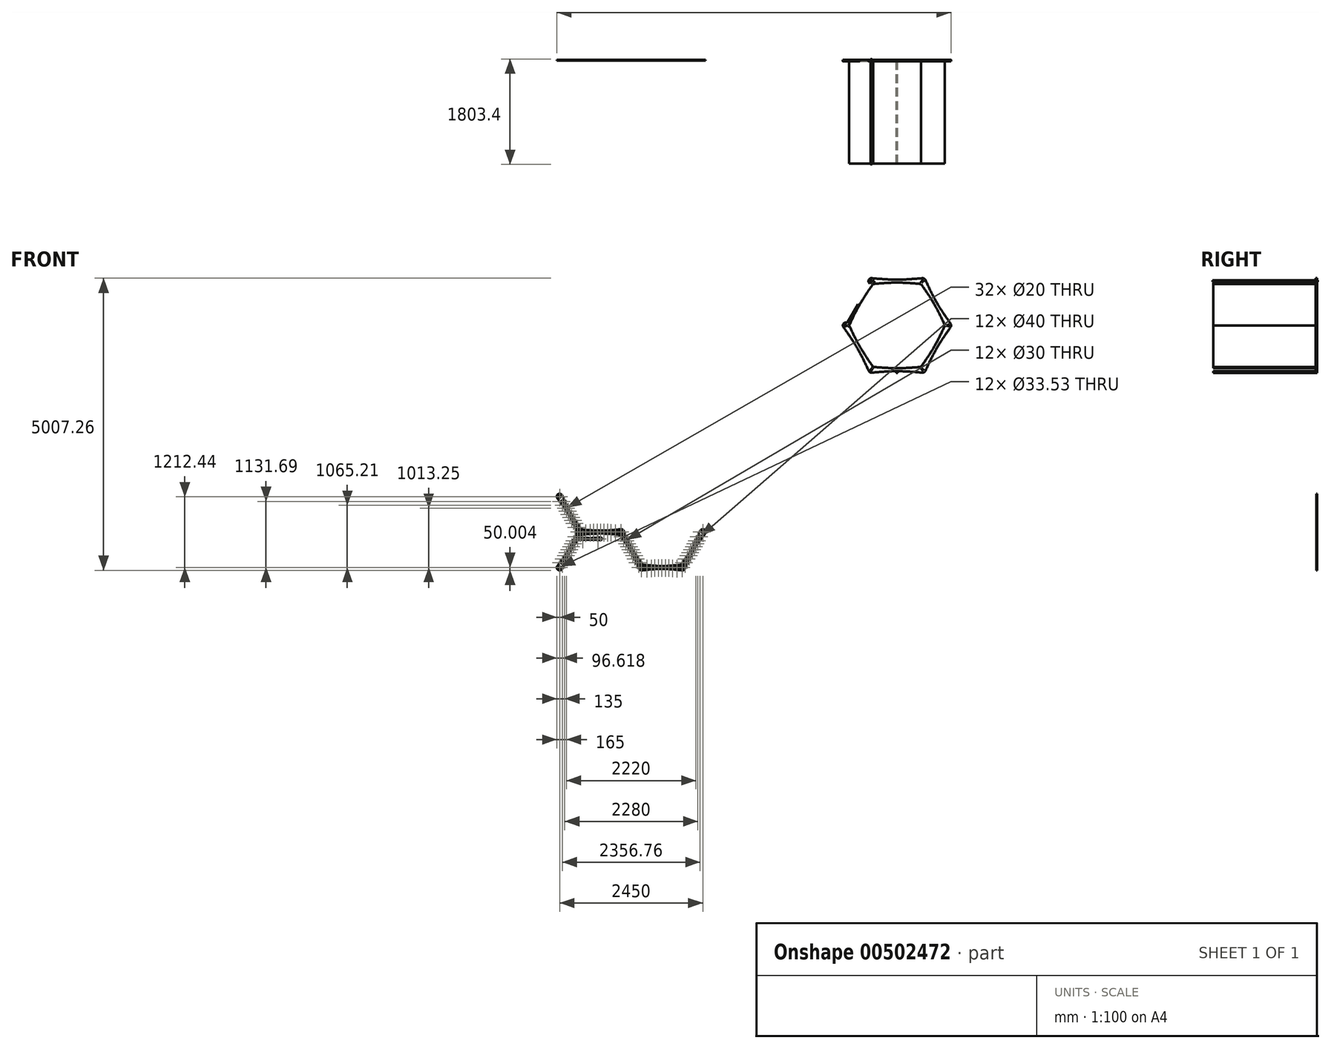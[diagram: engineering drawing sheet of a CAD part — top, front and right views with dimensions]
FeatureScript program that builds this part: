
annotation { "Feature Type Name" : "Feature", "Feature Type Description" : "" }
export const myFeature = defineFeature(function(context is Context, id is Id, definition is map)
    precondition{}
    {
        {
            var Q0;
            Q0=qCreatedBy(makeId("Front.planeOp"),FACE);
            var sketch = newSketch(context, id + "F0", { "sketchPlane" : qUnion([Q0])});
            skCircle(sketch, "E0", {"center": v(-63.33, -77.6) * mm, "radius": 25.4 * mm});
            skLineSegment(sketch, "E1", {"start": v(-63.33, -77.6) * mm, "end": v(286.67, -77.6) * mm});
            skLineSegment(sketch, "E2", {"start": v(-63.33, -77.6) * mm, "end": v(-88.73, -77.6) * mm});
            skLineSegment(sketch, "E3", {"start": v(-88.73, -77.6) * mm, "end": v(261.27, -77.6) * mm});
            skCircle(sketch, "E4", {"center": v(261.27, -77.6) * mm, "radius": 25.4 * mm});
            skLineSegment(sketch, "E5", {"start": v(86.27, -77.6) * mm, "end": v(86.27, -64.9) * mm});
            skLineSegment(sketch, "E6", {"start": v(86.27, -64.9) * mm, "end": v(86.27, -90.3) * mm});
            skCircle(sketch, "E7", {"center": v(0, 0) * mm, "radius": 25 * mm});
            skLineSegment(sketch, "E8", {"start": v(0, 0) * mm, "end": v(350, 0) * mm, "construction": true});
            skCircle(sketch, "E9", {"center": v(350, 0) * mm, "radius": 25 * mm});
            skLineSegment(sketch, "E10", {"start": v(175, 0) * mm, "end": v(175, -25) * mm, "construction": true});
            skFitSpline(sketch, "E11", {"points": [v(0, -25) * mm, v(175, -12.5) * mm, v(350, -25) * mm], "startDerivative": vector(350, 37.5) * mm, "endDerivative": vector(350, -37.5) * mm});
            skLineSegment(sketch, "E12", {"start": v(175, 0) * mm, "end": v(175, 25) * mm, "construction": true});
            skFitSpline(sketch, "E13", {"points": [v(0, 25) * mm, v(175, 12.5) * mm, v(350, 25) * mm], "startDerivative": vector(350, -37.5) * mm, "endDerivative": vector(350, 37.5) * mm});
            skCircle(sketch, "E14", {"center": v(350, 0) * mm, "radius": 8.38 * mm});
            skCircle(sketch, "E15", {"center": v(0, 0) * mm, "radius": 8.38 * mm});
            skCircle(sketch, "E16", {"center": v(175, 0) * mm, "radius": 5 * mm});
            skCircle(sketch, "E17.1.0.0", {"center": v(205, 0) * mm, "radius": 5 * mm});
            skCircle(sketch, "E17.2.0.0", {"center": v(235, 0) * mm, "radius": 5 * mm});
            skLineSegment(sketch, "E17.direction1", {"start": v(175, 0) * mm, "end": v(205, 0) * mm, "construction": true});
            skCircle(sketch, "E18.1.0.0", {"center": v(145, 0) * mm, "radius": 5 * mm});
            skCircle(sketch, "E18.2.0.0", {"center": v(115, 0) * mm, "radius": 5 * mm});
            skLineSegment(sketch, "E18.direction1", {"start": v(175, 0) * mm, "end": v(145, 0) * mm, "construction": true});
            skCircle(sketch, "E19", {"center": v(55, 0) * mm, "radius": 10 * mm});
            skCircle(sketch, "E20", {"center": v(85, 0) * mm, "radius": 7.5 * mm});
            skCircle(sketch, "E21.MirrorC", {"center": v(265, 0) * mm, "radius": 7.5 * mm});
            skCircle(sketch, "E22.MirrorC", {"center": v(295, 0) * mm, "radius": 10 * mm});
            skCircle(sketch, "E23", {"center": v(0, 115.33) * mm, "radius": 25 * mm});
            skLineSegment(sketch, "E24", {"start": v(0, 115.33) * mm, "end": v(350, 115.33) * mm, "construction": true});
            skCircle(sketch, "E25", {"center": v(350, 115.33) * mm, "radius": 25 * mm});
            skFitSpline(sketch, "E26", {"points": [v(0, 90.33) * mm, v(175, 102.83) * mm, v(350, 90.33) * mm], "startDerivative": vector(350, 37.5) * mm, "endDerivative": vector(350, -37.5) * mm});
            skFitSpline(sketch, "E27", {"points": [v(0, 140.33) * mm, v(175, 127.83) * mm, v(350, 140.33) * mm], "startDerivative": vector(350, -37.5) * mm, "endDerivative": vector(350, 37.5) * mm});
            skCircle(sketch, "E28", {"center": v(350, 115.33) * mm, "radius": 8.38 * mm});
            skCircle(sketch, "E29", {"center": v(0, 115.33) * mm, "radius": 8.38 * mm});
            skCircle(sketch, "E30", {"center": v(175, 115.33) * mm, "radius": 5 * mm});
            skCircle(sketch, "E31.1.0.0", {"center": v(205, 115.33) * mm, "radius": 5 * mm});
            skCircle(sketch, "E31.2.0.0", {"center": v(235, 115.33) * mm, "radius": 5 * mm});
            skLineSegment(sketch, "E31.direction1", {"start": v(175, 115.33) * mm, "end": v(205, 115.33) * mm, "construction": true});
            skCircle(sketch, "E32.1.0.0", {"center": v(145, 115.33) * mm, "radius": 5 * mm});
            skCircle(sketch, "E32.2.0.0", {"center": v(115, 115.33) * mm, "radius": 5 * mm});
            skLineSegment(sketch, "E32.direction1", {"start": v(175, 115.33) * mm, "end": v(145, 115.33) * mm, "construction": true});
            skCircle(sketch, "E33", {"center": v(46.62, 115.33) * mm, "radius": 10 * mm});
            skCircle(sketch, "E34", {"center": v(85, 115.33) * mm, "radius": 7.5 * mm});
            skCircle(sketch, "E35.MirrorC", {"center": v(265, 115.33) * mm, "radius": 7.5 * mm});
            skLineSegment(sketch, "E36", {"start": v(175, 102.83) * mm, "end": v(175, 127.83) * mm, "construction": true});
            skCircle(sketch, "E37.MirrorC", {"center": v(303.38, 115.33) * mm, "radius": 10 * mm});
            skCircle(sketch, "E38", {"center": v(-2662.95, -296.07) * mm, "radius": 25 * mm});
            skLineSegment(sketch, "E39", {"start": v(-2662.95, -296.07) * mm, "end": v(-2359.84, -121.07) * mm, "construction": true});
            skCircle(sketch, "E40", {"center": v(-2359.84, -121.07) * mm, "radius": 25 * mm});
            skFitSpline(sketch, "E41", {"points": [v(-2650.45, -317.72) * mm, v(-2505.15, -219.4) * mm, v(-2347.34, -142.72) * mm], "startDerivative": vector(284.36, 207.48) * mm, "endDerivative": vector(321.86, 142.52) * mm});
            skFitSpline(sketch, "E42", {"points": [v(-2675.45, -274.42) * mm, v(-2517.65, -197.74) * mm, v(-2372.34, -99.42) * mm], "startDerivative": vector(321.86, 142.52) * mm, "endDerivative": vector(284.36, 207.48) * mm});
            skCircle(sketch, "E43", {"center": v(-2359.84, -121.07) * mm, "radius": 8.38 * mm});
            skCircle(sketch, "E44", {"center": v(-2662.95, -296.07) * mm, "radius": 8.38 * mm});
            skCircle(sketch, "E45", {"center": v(-2511.4, -208.57) * mm, "radius": 5 * mm});
            skCircle(sketch, "E46.1.0.0", {"center": v(-2485.42, -193.57) * mm, "radius": 5 * mm});
            skCircle(sketch, "E46.2.0.0", {"center": v(-2459.43, -178.57) * mm, "radius": 5 * mm});
            skLineSegment(sketch, "E46.direction1", {"start": v(-2511.4, -208.57) * mm, "end": v(-2485.42, -193.57) * mm, "construction": true});
            skCircle(sketch, "E47.1.0.0", {"center": v(-2537.38, -223.57) * mm, "radius": 5 * mm});
            skCircle(sketch, "E47.2.0.0", {"center": v(-2563.36, -238.57) * mm, "radius": 5 * mm});
            skLineSegment(sketch, "E47.direction1", {"start": v(-2511.4, -208.57) * mm, "end": v(-2537.38, -223.57) * mm, "construction": true});
            skCircle(sketch, "E48", {"center": v(-2622.58, -272.76) * mm, "radius": 10 * mm});
            skCircle(sketch, "E49", {"center": v(-2589.34, -253.57) * mm, "radius": 7.5 * mm});
            skCircle(sketch, "E50.MirrorC", {"center": v(-2433.45, -163.57) * mm, "radius": 7.5 * mm});
            skLineSegment(sketch, "E51", {"start": v(-2505.15, -219.4) * mm, "end": v(-2517.65, -197.74) * mm, "construction": true});
            skCircle(sketch, "E52.MirrorC", {"center": v(-2400.21, -144.38) * mm, "radius": 10 * mm});
            skLineSegment(sketch, "E53.0", {"start": v(-2347.34, -142.72) * mm, "end": v(-2372.34, -99.42) * mm, "construction": true});
            skLineSegment(sketch, "E54", {"start": v(-2359.84, -121.07) * mm, "end": v(-2056.73, 53.93) * mm, "construction": true});
            skCircle(sketch, "E55", {"center": v(-2056.73, 53.93) * mm, "radius": 25 * mm});
            skFitSpline(sketch, "E56", {"points": [v(-2347.34, -142.72) * mm, v(-2202.04, -44.4) * mm, v(-2044.23, 32.28) * mm], "startDerivative": vector(284.36, 207.48) * mm, "endDerivative": vector(321.86, 142.52) * mm});
            skFitSpline(sketch, "E57", {"points": [v(-2372.34, -99.42) * mm, v(-2214.54, -22.74) * mm, v(-2069.23, 75.58) * mm], "startDerivative": vector(321.86, 142.52) * mm, "endDerivative": vector(284.36, 207.48) * mm});
            skCircle(sketch, "E58", {"center": v(-2056.73, 53.93) * mm, "radius": 8.38 * mm});
            skCircle(sketch, "E59", {"center": v(-2208.29, -33.57) * mm, "radius": 5 * mm});
            skCircle(sketch, "E60.1.0.0", {"center": v(-2182.3, -18.57) * mm, "radius": 5 * mm});
            skCircle(sketch, "E60.2.0.0", {"center": v(-2156.33, -3.57) * mm, "radius": 5 * mm});
            skLineSegment(sketch, "E60.direction1", {"start": v(-2208.29, -33.57) * mm, "end": v(-2182.3, -18.57) * mm, "construction": true});
            skCircle(sketch, "E61.1.0.0", {"center": v(-2234.27, -48.57) * mm, "radius": 5 * mm});
            skCircle(sketch, "E61.2.0.0", {"center": v(-2260.25, -63.57) * mm, "radius": 5 * mm});
            skLineSegment(sketch, "E61.direction1", {"start": v(-2208.29, -33.57) * mm, "end": v(-2234.27, -48.57) * mm, "construction": true});
            skCircle(sketch, "E62", {"center": v(-2319.47, -97.76) * mm, "radius": 10 * mm});
            skCircle(sketch, "E63", {"center": v(-2286.23, -78.57) * mm, "radius": 7.5 * mm});
            skCircle(sketch, "E64.MirrorC", {"center": v(-2130.34, 11.43) * mm, "radius": 7.5 * mm});
            skLineSegment(sketch, "E65", {"start": v(-2202.04, -44.4) * mm, "end": v(-2214.54, -22.74) * mm, "construction": true});
            skCircle(sketch, "E66.MirrorC", {"center": v(-2097.1, 30.62) * mm, "radius": 10 * mm});
            skLineSegment(sketch, "E67.0", {"start": v(-2044.23, 32.28) * mm, "end": v(-2069.23, 75.58) * mm, "construction": true});
            skSolve(sketch);
        }
        {
            var Q0;
            Q0=qCreatedBy(makeId("Front.planeOp"),FACE);
            var sketch = newSketch(context, id + "F1", { "sketchPlane" : qUnion([Q0])});
            skLineSegment(sketch, "E68.bottom", {"start": v(431.16, -314.1) * mm, "end": v(2869.56, -314.1) * mm});
            skLineSegment(sketch, "E68.top", {"start": v(431.16, 2124.3) * mm, "end": v(2869.56, 2124.3) * mm});
            skLineSegment(sketch, "E68.left", {"start": v(431.16, -314.1) * mm, "end": v(431.16, 2124.3) * mm});
            skLineSegment(sketch, "E68.right", {"start": v(2869.56, -314.1) * mm, "end": v(2869.56, 2124.3) * mm});
            skLineSegment(sketch, "E69", {"start": v(431.16, 905.1) * mm, "end": v(2869.56, 905.1) * mm, "construction": true});
            skCircle(sketch, "E70.cCircle", {"center": v(1197.59, 279.82) * mm, "radius": 593.92 * mm, "construction": true});
            skLineSegment(sketch, "E70.0", {"start": v(1540.49, -314.1) * mm, "end": v(854.69, -314.1) * mm, "construction": true});
            skLineSegment(sketch, "E70.1", {"start": v(854.69, -314.1) * mm, "end": v(511.79, 279.82) * mm, "construction": true});
            skLineSegment(sketch, "E70.2", {"start": v(511.79, 279.82) * mm, "end": v(854.69, 873.74) * mm, "construction": true});
            skLineSegment(sketch, "E70.3", {"start": v(854.69, 873.74) * mm, "end": v(1540.49, 873.74) * mm, "construction": true});
            skLineSegment(sketch, "E70.4", {"start": v(1540.49, 873.74) * mm, "end": v(1883.39, 279.82) * mm, "construction": true});
            skLineSegment(sketch, "E70.5", {"start": v(1883.39, 279.82) * mm, "end": v(1540.49, -314.1) * mm, "construction": true});
            skPoint(sketch, "E70.0.midPoint", {"position": v(1197.59, -314.1) * mm});
            skCircle(sketch, "E71.cCircle", {"center": v(2647.5, 295.5) * mm, "radius": 527.93 * mm, "construction": true});
            skLineSegment(sketch, "E71.0", {"start": v(3175.44, 600.3) * mm, "end": v(3175.44, -9.3) * mm});
            skLineSegment(sketch, "E71.1", {"start": v(3175.44, -9.3) * mm, "end": v(2647.5, -314.1) * mm});
            skLineSegment(sketch, "E71.2", {"start": v(2647.5, -314.1) * mm, "end": v(2119.58, -9.3) * mm});
            skLineSegment(sketch, "E71.3", {"start": v(2119.58, -9.3) * mm, "end": v(2119.58, 600.3) * mm});
            skLineSegment(sketch, "E71.4", {"start": v(2119.58, 600.3) * mm, "end": v(2647.5, 905.1) * mm});
            skLineSegment(sketch, "E71.5", {"start": v(2647.5, 905.1) * mm, "end": v(3175.44, 600.3) * mm});
            skPoint(sketch, "E71.0.midPoint", {"position": v(3175.44, 295.5) * mm});
            skCircle(sketch, "E72.cCircle", {"center": v(4442.22, 446.69) * mm, "radius": 703.9 * mm, "construction": true});
            skLineSegment(sketch, "E72.0", {"start": v(4442.22, -366.11) * mm, "end": v(3738.32, 40.29) * mm});
            skLineSegment(sketch, "E72.1", {"start": v(3738.32, 40.29) * mm, "end": v(3738.32, 853.09) * mm});
            skLineSegment(sketch, "E72.2", {"start": v(3738.32, 853.09) * mm, "end": v(4442.22, 1259.49) * mm});
            skLineSegment(sketch, "E72.3", {"start": v(4442.22, 1259.49) * mm, "end": v(5146.13, 853.09) * mm});
            skLineSegment(sketch, "E72.4", {"start": v(5146.13, 853.09) * mm, "end": v(5146.13, 40.29) * mm});
            skLineSegment(sketch, "E72.5", {"start": v(5146.13, 40.29) * mm, "end": v(4442.22, -366.11) * mm});
            skPoint(sketch, "E72.0.midPoint", {"position": v(4090.27, -162.91) * mm});
            skLineSegment(sketch, "E73.0", {"start": v(5146.13, 853.09) * mm, "end": v(4442.22, 1259.49) * mm});
            skLineSegment(sketch, "E73.1", {"start": v(4442.22, 1259.49) * mm, "end": v(4442.22, 2072.29) * mm});
            skLineSegment(sketch, "E73.2", {"start": v(4442.22, 2072.29) * mm, "end": v(5146.13, 2478.69) * mm});
            skLineSegment(sketch, "E73.3", {"start": v(5146.13, 2478.69) * mm, "end": v(5850.03, 2072.29) * mm});
            skLineSegment(sketch, "E73.4", {"start": v(5850.03, 2072.29) * mm, "end": v(5850.03, 1259.49) * mm});
            skLineSegment(sketch, "E73.5", {"start": v(5850.03, 1259.49) * mm, "end": v(5146.13, 853.09) * mm});
            skLineSegment(sketch, "E74.0", {"start": v(3175.44, 1819.5) * mm, "end": v(3175.44, 1209.9) * mm});
            skLineSegment(sketch, "E74.1", {"start": v(3175.44, 1209.9) * mm, "end": v(2647.5, 905.1) * mm});
            skLineSegment(sketch, "E74.2", {"start": v(2647.5, 905.1) * mm, "end": v(2119.58, 1209.9) * mm});
            skLineSegment(sketch, "E74.3", {"start": v(2119.58, 1209.9) * mm, "end": v(2119.58, 1819.5) * mm});
            skLineSegment(sketch, "E74.4", {"start": v(2119.58, 1819.5) * mm, "end": v(2647.5, 2124.3) * mm});
            skLineSegment(sketch, "E74.5", {"start": v(2647.5, 2124.3) * mm, "end": v(3175.44, 1819.5) * mm});
            skLineSegment(sketch, "E75.bottom", {"start": v(-3848.6, -370.11) * mm, "end": v(-6287, -370.11) * mm});
            skLineSegment(sketch, "E75.top", {"start": v(-3848.6, 2068.29) * mm, "end": v(-6287, 2068.29) * mm});
            skLineSegment(sketch, "E75.right", {"start": v(-6287, -370.11) * mm, "end": v(-6287, 2068.29) * mm});
            skLineSegment(sketch, "E76", {"start": v(-6287, 849.09) * mm, "end": v(-3848.6, 849.09) * mm, "construction": true});
            skCircle(sketch, "E77.cCircle", {"center": v(-6287, 315.69) * mm, "radius": 685.8 * mm, "construction": true});
            skPoint(sketch, "E77.cCircle.perimeterSnap0", {"position": v(-5067.8, -370.11) * mm});
            skLineSegment(sketch, "E77.0", {"start": v(-6287, -370.11) * mm, "end": v(-6880.91, -27.21) * mm});
            skPoint(sketch, "E77.0.startSnap0", {"position": v(-5067.8, -370.11) * mm});
            skLineSegment(sketch, "E77.1", {"start": v(-6880.91, -27.21) * mm, "end": v(-6880.91, 658.59) * mm});
            skLineSegment(sketch, "E77.2", {"start": v(-6880.91, 658.59) * mm, "end": v(-6287, 1001.49) * mm});
            skLineSegment(sketch, "E77.3", {"start": v(-6287, 1001.49) * mm, "end": v(-5693.07, 658.59) * mm});
            skLineSegment(sketch, "E77.4", {"start": v(-5693.07, 658.59) * mm, "end": v(-5693.07, -27.21) * mm});
            skLineSegment(sketch, "E77.5", {"start": v(-5693.07, -27.21) * mm, "end": v(-6287, -370.11) * mm});
            skCircle(sketch, "E78.cCircle", {"center": v(-5693.07, 1344.39) * mm, "radius": 685.8 * mm, "construction": true});
            skLineSegment(sketch, "E78.0", {"start": v(-5693.07, 658.59) * mm, "end": v(-6287, 1001.49) * mm});
            skLineSegment(sketch, "E78.1", {"start": v(-6287, 1001.49) * mm, "end": v(-6287, 1687.29) * mm});
            skLineSegment(sketch, "E78.2", {"start": v(-6287, 1687.29) * mm, "end": v(-5693.07, 2030.19) * mm});
            skLineSegment(sketch, "E78.3", {"start": v(-5693.07, 2030.19) * mm, "end": v(-5099.15, 1687.29) * mm});
            skLineSegment(sketch, "E78.4", {"start": v(-5099.15, 1687.29) * mm, "end": v(-5099.15, 1001.49) * mm});
            skLineSegment(sketch, "E78.5", {"start": v(-5099.15, 1001.49) * mm, "end": v(-5693.07, 658.59) * mm});
            skLineSegment(sketch, "E79.0", {"start": v(-5099.15, -370.11) * mm, "end": v(-5693.07, -27.21) * mm});
            skLineSegment(sketch, "E79.1", {"start": v(-5693.07, -27.21) * mm, "end": v(-5693.07, 658.59) * mm});
            skLineSegment(sketch, "E79.2", {"start": v(-5693.07, 658.59) * mm, "end": v(-5099.15, 1001.49) * mm});
            skLineSegment(sketch, "E79.3", {"start": v(-5099.15, 1001.49) * mm, "end": v(-4505.23, 658.59) * mm});
            skLineSegment(sketch, "E79.4", {"start": v(-4505.23, 658.59) * mm, "end": v(-4505.23, -27.21) * mm});
            skLineSegment(sketch, "E79.5", {"start": v(-4505.23, -27.21) * mm, "end": v(-5099.15, -370.11) * mm});
            skLineSegment(sketch, "E80.0", {"start": v(-4505.23, 658.59) * mm, "end": v(-5099.15, 1001.49) * mm});
            skLineSegment(sketch, "E81.1", {"start": v(-5099.15, 1001.49) * mm, "end": v(-5099.15, 1687.29) * mm});
            skLineSegment(sketch, "E81.2", {"start": v(-5099.15, 1687.29) * mm, "end": v(-4505.23, 2030.19) * mm});
            skLineSegment(sketch, "E81.3", {"start": v(-4505.23, 2030.19) * mm, "end": v(-3911.31, 1687.29) * mm});
            skLineSegment(sketch, "E81.4", {"start": v(-3911.31, 1687.29) * mm, "end": v(-3911.31, 1001.49) * mm});
            skLineSegment(sketch, "E81.5", {"start": v(-3911.31, 1001.49) * mm, "end": v(-4505.23, 658.59) * mm});
            skLineSegment(sketch, "E82.0", {"start": v(-3911.31, 1687.29) * mm, "end": v(-4505.23, 2030.19) * mm});
            skLineSegment(sketch, "E83.0", {"start": v(-3911.31, -370.11) * mm, "end": v(-4505.23, -27.21) * mm});
            skLineSegment(sketch, "E83.1", {"start": v(-4505.23, -27.21) * mm, "end": v(-4505.23, 658.59) * mm});
            skLineSegment(sketch, "E83.2", {"start": v(-4505.23, 658.59) * mm, "end": v(-3911.31, 1001.49) * mm});
            skLineSegment(sketch, "E83.3", {"start": v(-3911.31, 1001.49) * mm, "end": v(-3317.4, 658.59) * mm});
            skLineSegment(sketch, "E83.4", {"start": v(-3317.4, 658.59) * mm, "end": v(-3317.4, -27.21) * mm});
            skLineSegment(sketch, "E83.5", {"start": v(-3317.4, -27.21) * mm, "end": v(-3911.31, -370.11) * mm});
            skLineSegment(sketch, "E84.0", {"start": v(-3317.4, 658.59) * mm, "end": v(-3911.31, 1001.49) * mm});
            skLineSegment(sketch, "E85", {"start": v(604.84, 118.65) * mm, "end": v(1792.3, 118.65) * mm, "construction": true});
            skLineSegment(sketch, "E86", {"start": v(-4505.23, -27.21) * mm, "end": v(-4505.23, -370.11) * mm});
            skLineSegment(sketch, "E87", {"start": v(-5099.15, -370.11) * mm, "end": v(-4505.23, -370.11) * mm});
            skLineSegment(sketch, "E88", {"start": v(-4802.2, -370.11) * mm, "end": v(-4802.2, -198.66) * mm});
            skLineSegment(sketch, "E89", {"start": v(-5099.15, 1687.29) * mm, "end": v(-3911.31, 1687.29) * mm});
            skLineSegment(sketch, "E90", {"start": v(-4505.23, 2030.19) * mm, "end": v(-3911.31, 1001.49) * mm});
            skLineSegment(sketch, "E91", {"start": v(-3911.31, 1687.29) * mm, "end": v(-4505.23, 658.59) * mm});
            skLineSegment(sketch, "E92", {"start": v(-3911.31, 1001.49) * mm, "end": v(-5099.15, 1001.49) * mm});
            skLineSegment(sketch, "E93", {"start": v(-4505.23, 658.59) * mm, "end": v(-5099.15, 1687.29) * mm});
            skLineSegment(sketch, "E94", {"start": v(-5099.15, 1001.49) * mm, "end": v(-4505.23, 2030.19) * mm});
            skLineSegment(sketch, "E95", {"start": v(-4505.23, 658.59) * mm, "end": v(-3911.31, -370.11) * mm});
            skLineSegment(sketch, "E96", {"start": v(-4505.23, 658.59) * mm, "end": v(-3317.4, -27.21) * mm});
            skLineSegment(sketch, "E97", {"start": v(-4505.23, 658.59) * mm, "end": v(-3317.4, 658.59) * mm});
            skLineSegment(sketch, "E98", {"start": v(-4505.23, -27.21) * mm, "end": v(-3911.31, 1001.49) * mm});
            skLineSegment(sketch, "E99", {"start": v(-4505.23, -27.21) * mm, "end": v(-3317.4, 658.59) * mm});
            skLineSegment(sketch, "E100", {"start": v(-4505.23, -27.21) * mm, "end": v(-3317.4, -27.21) * mm});
            skLineSegment(sketch, "E101", {"start": v(-3911.31, -370.11) * mm, "end": v(-3911.31, 1001.49) * mm});
            skLineSegment(sketch, "E102", {"start": v(-3911.31, -370.11) * mm, "end": v(-3317.4, 658.59) * mm});
            skLineSegment(sketch, "E103", {"start": v(-3317.4, -27.21) * mm, "end": v(-4505.23, -27.21) * mm});
            skLineSegment(sketch, "E104", {"start": v(-3317.4, -27.21) * mm, "end": v(-3911.31, 1001.49) * mm});
            skLineSegment(sketch, "E105", {"start": v(854.69, -314.1) * mm, "end": v(1883.39, 279.82) * mm});
            skLineSegment(sketch, "E106", {"start": v(1540.49, -314.1) * mm, "end": v(511.79, 279.82) * mm});
            skLineSegment(sketch, "E107", {"start": v(854.69, -314.1) * mm, "end": v(854.69, 873.74) * mm});
            skLineSegment(sketch, "E108", {"start": v(511.79, 279.82) * mm, "end": v(1540.49, 873.74) * mm});
            skLineSegment(sketch, "E109", {"start": v(854.69, 873.74) * mm, "end": v(1883.39, 279.82) * mm});
            skLineSegment(sketch, "E110", {"start": v(1540.49, 873.74) * mm, "end": v(1540.49, -314.1) * mm});
            skLineSegment(sketch, "E111", {"start": v(-6287, 1001.49) * mm, "end": v(-5693.07, 2030.19) * mm});
            skLineSegment(sketch, "E112", {"start": v(-5693.07, 2030.19) * mm, "end": v(-5099.15, 1001.49) * mm});
            skLineSegment(sketch, "E113", {"start": v(-5099.15, 1001.49) * mm, "end": v(-6287, 1001.49) * mm});
            skCircle(sketch, "E114", {"center": v(-3216.09, 1940.13) * mm, "radius": 6.35 * mm});
            skCircle(sketch, "E115.cCircle", {"center": v(-1877.48, 3384.74) * mm, "radius": 538.93 * mm, "construction": true});
            skLineSegment(sketch, "E115.0", {"start": v(-2416.4, 3073.59) * mm, "end": v(-2416.4, 3695.89) * mm});
            skLineSegment(sketch, "E115.1", {"start": v(-2416.4, 3695.89) * mm, "end": v(-1877.48, 4007.04) * mm});
            skLineSegment(sketch, "E115.2", {"start": v(-1877.48, 4007.04) * mm, "end": v(-1338.55, 3695.89) * mm});
            skLineSegment(sketch, "E115.3", {"start": v(-1338.55, 3695.89) * mm, "end": v(-1338.55, 3073.59) * mm});
            skLineSegment(sketch, "E115.4", {"start": v(-1338.55, 3073.59) * mm, "end": v(-1877.48, 2762.44) * mm});
            skLineSegment(sketch, "E115.5", {"start": v(-1877.48, 2762.44) * mm, "end": v(-2416.4, 3073.59) * mm});
            skPoint(sketch, "E115.0.midPoint", {"position": v(-2416.4, 3384.74) * mm});
            skCircle(sketch, "E116.cCircle", {"center": v(-1338.55, 4318.19) * mm, "radius": 538.93 * mm, "construction": true});
            skLineSegment(sketch, "E116.0", {"start": v(-1877.48, 4007.04) * mm, "end": v(-1877.48, 4629.34) * mm});
            skLineSegment(sketch, "E116.1", {"start": v(-1877.48, 4629.34) * mm, "end": v(-1338.55, 4940.49) * mm});
            skLineSegment(sketch, "E116.2", {"start": v(-1338.55, 4940.49) * mm, "end": v(-799.62, 4629.34) * mm});
            skLineSegment(sketch, "E116.3", {"start": v(-799.62, 4629.34) * mm, "end": v(-799.62, 4007.04) * mm});
            skLineSegment(sketch, "E116.4", {"start": v(-799.62, 4007.04) * mm, "end": v(-1338.55, 3695.89) * mm});
            skLineSegment(sketch, "E116.5", {"start": v(-1338.55, 3695.89) * mm, "end": v(-1877.48, 4007.04) * mm});
            skPoint(sketch, "E116.0.midPoint", {"position": v(-1877.48, 4318.19) * mm});
            skCircle(sketch, "E117.cCircle", {"center": v(-799.62, 3384.74) * mm, "radius": 538.93 * mm, "construction": true});
            skLineSegment(sketch, "E117.0", {"start": v(-1338.55, 3073.59) * mm, "end": v(-1338.55, 3695.89) * mm});
            skLineSegment(sketch, "E117.1", {"start": v(-1338.55, 3695.89) * mm, "end": v(-799.62, 4007.04) * mm});
            skLineSegment(sketch, "E117.2", {"start": v(-799.62, 4007.04) * mm, "end": v(-260.7, 3695.89) * mm});
            skLineSegment(sketch, "E117.3", {"start": v(-260.7, 3695.89) * mm, "end": v(-260.7, 3073.59) * mm});
            skLineSegment(sketch, "E117.4", {"start": v(-260.7, 3073.59) * mm, "end": v(-799.62, 2762.44) * mm});
            skLineSegment(sketch, "E117.5", {"start": v(-799.62, 2762.44) * mm, "end": v(-1338.55, 3073.59) * mm});
            skPoint(sketch, "E117.0.midPoint", {"position": v(-1338.55, 3384.74) * mm});
            skCircle(sketch, "E118", {"center": v(-2416.4, 3073.59) * mm, "radius": 12.7 * mm});
            skCircle(sketch, "E119", {"center": v(-2416.4, 3073.59) * mm, "radius": 50.8 * mm});
            skCircle(sketch, "E120", {"center": v(-2416.4, 3695.89) * mm, "radius": 50.8 * mm});
            skCircle(sketch, "E121", {"center": v(-2416.4, 3695.89) * mm, "radius": 12.7 * mm});
            skCircle(sketch, "E122", {"center": v(-2416.4, 3384.74) * mm, "radius": 6.35 * mm});
            skCircle(sketch, "E123", {"center": v(-2416.4, 3384.74) * mm, "radius": 25.4 * mm});
            skFitSpline(sketch, "E124", {"points": [v(-2467.2, 3695.89) * mm, v(-2441.8, 3384.74) * mm, v(-2467.2, 3073.59) * mm], "startDerivative": vector(69.83, -634.43) * mm, "endDerivative": vector(-44.45, -635.57) * mm});
            skFitSpline(sketch, "E125", {"points": [v(-2365.6, 3695.89) * mm, v(-2391, 3384.74) * mm, v(-2365.6, 3073.59) * mm], "startDerivative": vector(-76.2, -635) * mm, "endDerivative": vector(76.2, -635) * mm});
            skCircle(sketch, "E126", {"center": v(-1877.48, 2762.44) * mm, "radius": 12.7 * mm});
            skCircle(sketch, "E127", {"center": v(-1877.48, 2762.44) * mm, "radius": 50.8 * mm});
            skCircle(sketch, "E128", {"center": v(-1338.55, 3073.59) * mm, "radius": 50.8 * mm});
            skCircle(sketch, "E129", {"center": v(-1338.55, 3073.59) * mm, "radius": 12.7 * mm});
            skCircle(sketch, "E130", {"center": v(-1608.01, 2918.01) * mm, "radius": 6.35 * mm});
            skCircle(sketch, "E131", {"center": v(-1608.01, 2918.01) * mm, "radius": 25.4 * mm});
            skFitSpline(sketch, "E132", {"points": [v(-1363.95, 3117.58) * mm, v(-1620.71, 2940) * mm, v(-1902.88, 2806.43) * mm], "startDerivative": vector(-514.52, -377.69) * mm, "endDerivative": vector(-572.64, -279.29) * mm});
            skFitSpline(sketch, "E133", {"points": [v(-1313.15, 3029.6) * mm, v(-1595.31, 2896.01) * mm, v(-1852.08, 2718.44) * mm], "startDerivative": vector(-588.03, -251.5) * mm, "endDerivative": vector(-511.83, -383.5) * mm});
            skCircle(sketch, "E134", {"center": v(-1338.55, 4940.49) * mm, "radius": 12.7 * mm});
            skCircle(sketch, "E135", {"center": v(-1338.55, 4940.49) * mm, "radius": 50.8 * mm});
            skCircle(sketch, "E136", {"center": v(-799.62, 4629.34) * mm, "radius": 50.8 * mm});
            skCircle(sketch, "E137", {"center": v(-799.62, 4629.34) * mm, "radius": 12.7 * mm});
            skCircle(sketch, "E138", {"center": v(-1069.08, 4784.91) * mm, "radius": 6.35 * mm});
            skCircle(sketch, "E139", {"center": v(-1069.08, 4784.91) * mm, "radius": 25.4 * mm});
            skFitSpline(sketch, "E140", {"points": [v(-774.22, 4673.33) * mm, v(-1056.38, 4806.9) * mm, v(-1313.15, 4984.48) * mm], "startDerivative": vector(-584.35, 256.74) * mm, "endDerivative": vector(-528.2, 356.28) * mm});
            skFitSpline(sketch, "E141", {"points": [v(-825.02, 4585.34) * mm, v(-1081.78, 4762.91) * mm, v(-1363.95, 4896.5) * mm], "startDerivative": vector(-511.83, 383.5) * mm, "endDerivative": vector(-588.03, 251.5) * mm});
            skCircle(sketch, "E142", {"center": v(-1877.48, 4007.04) * mm, "radius": 50.8 * mm});
            skCircle(sketch, "E143", {"center": v(-1877.48, 4007.04) * mm, "radius": 12.7 * mm});
            skCircle(sketch, "E144", {"center": v(-2146.94, 3851.46) * mm, "radius": 6.35 * mm});
            skCircle(sketch, "E145", {"center": v(-2146.94, 3851.46) * mm, "radius": 25.4 * mm});
            skFitSpline(sketch, "E146", {"points": [v(-1902.88, 4051.03) * mm, v(-2159.64, 3873.46) * mm, v(-2441.8, 3739.88) * mm], "startDerivative": vector(-514.52, -377.69) * mm, "endDerivative": vector(-572.64, -279.29) * mm});
            skFitSpline(sketch, "E147", {"points": [v(-1852.08, 3963.04) * mm, v(-2134.24, 3829.46) * mm, v(-2391, 3651.9) * mm], "startDerivative": vector(-588.03, -251.5) * mm, "endDerivative": vector(-511.83, -383.5) * mm});
            skCircle(sketch, "E148", {"center": v(-1338.55, 3695.89) * mm, "radius": 50.8 * mm});
            skCircle(sketch, "E149", {"center": v(-1338.55, 3695.89) * mm, "radius": 12.7 * mm});
            skCircle(sketch, "E150", {"center": v(-1338.55, 3384.74) * mm, "radius": 6.35 * mm});
            skCircle(sketch, "E151", {"center": v(-1338.55, 3384.74) * mm, "radius": 25.4 * mm});
            skFitSpline(sketch, "E152", {"points": [v(-1389.35, 3695.89) * mm, v(-1363.95, 3384.74) * mm, v(-1389.35, 3073.59) * mm], "startDerivative": vector(69.83, -634.43) * mm, "endDerivative": vector(-44.45, -635.57) * mm});
            skFitSpline(sketch, "E153", {"points": [v(-1287.75, 3695.89) * mm, v(-1313.15, 3384.74) * mm, v(-1287.75, 3073.59) * mm], "startDerivative": vector(-76.2, -635) * mm, "endDerivative": vector(76.2, -635) * mm});
            skCircle(sketch, "E154", {"center": v(-2146.94, 2918.01) * mm, "radius": 6.35 * mm});
            skCircle(sketch, "E155", {"center": v(-2146.94, 2918.01) * mm, "radius": 25.4 * mm});
            skFitSpline(sketch, "E156", {"points": [v(-1852.08, 2806.43) * mm, v(-2134.24, 2940) * mm, v(-2391, 3117.58) * mm], "startDerivative": vector(-584.35, 256.74) * mm, "endDerivative": vector(-528.2, 356.28) * mm});
            skFitSpline(sketch, "E157", {"points": [v(-1902.88, 2718.44) * mm, v(-2159.64, 2896.01) * mm, v(-2441.8, 3029.6) * mm], "startDerivative": vector(-511.83, 383.5) * mm, "endDerivative": vector(-588.03, 251.5) * mm});
            skCircle(sketch, "E158", {"center": v(-1608.01, 3851.46) * mm, "radius": 6.35 * mm});
            skCircle(sketch, "E159", {"center": v(-1608.01, 3851.46) * mm, "radius": 25.4 * mm});
            skFitSpline(sketch, "E160", {"points": [v(-1313.15, 3739.88) * mm, v(-1595.31, 3873.46) * mm, v(-1852.08, 4051.03) * mm], "startDerivative": vector(-584.35, 256.74) * mm, "endDerivative": vector(-528.2, 356.28) * mm});
            skFitSpline(sketch, "E161", {"points": [v(-1363.95, 3651.9) * mm, v(-1620.71, 3829.46) * mm, v(-1902.88, 3963.04) * mm], "startDerivative": vector(-511.83, 383.5) * mm, "endDerivative": vector(-588.03, 251.5) * mm});
            skLineSegment(sketch, "E162", {"start": v(-2042.65, 2711.64) * mm, "end": v(-1559.7, 2711.64) * mm, "construction": true});
            skLineSegment(sketch, "E163", {"start": v(-1859.2, 4991.29) * mm, "end": v(-103.87, 4991.29) * mm, "construction": true});
            skLineSegment(sketch, "E164", {"start": v(-1877.48, 3952.18) * mm, "end": v(-2644.2, 3952.18) * mm, "construction": true});
            skLineSegment(sketch, "E165", {"start": v(-2369.08, 3102.57) * mm, "end": v(-2672.1, 3102.57) * mm, "construction": true});
            skLineSegment(sketch, "E166.bottom", {"start": v(3332.13, 3772) * mm, "end": v(5770.53, 3772) * mm, "construction": true});
            skLineSegment(sketch, "E166.top", {"start": v(3332.13, 2959.2) * mm, "end": v(5770.53, 2959.2) * mm, "construction": true});
            skLineSegment(sketch, "E166.left", {"start": v(3332.13, 3772) * mm, "end": v(3332.13, 2959.2) * mm, "construction": true});
            skLineSegment(sketch, "E166.right", {"start": v(5770.53, 3772) * mm, "end": v(5770.53, 2959.2) * mm, "construction": true});
            skLineSegment(sketch, "E167", {"start": v(3332.13, 3772) * mm, "end": v(3332.13, 4584.8) * mm, "construction": true});
            skLineSegment(sketch, "E168", {"start": v(3332.13, 4584.8) * mm, "end": v(3332.13, 5397.6) * mm, "construction": true});
            skCircle(sketch, "E169.cCircle", {"center": v(4111.37, 4530.9) * mm, "radius": 758.9 * mm, "construction": true});
            skLineSegment(sketch, "E169.0", {"start": v(4549.52, 3772) * mm, "end": v(3673.22, 3772) * mm});
            skLineSegment(sketch, "E169.1", {"start": v(3673.22, 3772) * mm, "end": v(3235.07, 4530.9) * mm});
            skLineSegment(sketch, "E169.2", {"start": v(3235.07, 4530.9) * mm, "end": v(3673.22, 5289.8) * mm});
            skLineSegment(sketch, "E169.3", {"start": v(3673.22, 5289.8) * mm, "end": v(4549.52, 5289.8) * mm});
            skLineSegment(sketch, "E169.4", {"start": v(4549.52, 5289.8) * mm, "end": v(4987.67, 4530.9) * mm});
            skLineSegment(sketch, "E169.5", {"start": v(4987.67, 4530.9) * mm, "end": v(4549.52, 3772) * mm});
            skPoint(sketch, "E169.0.midPoint", {"position": v(4111.37, 3772) * mm});
            skPoint(sketch, "E170.0.midPoint", {"position": v(5456.94, 2905.3) * mm});
            skCircle(sketch, "E171", {"center": v(3673.22, 5289.8) * mm, "radius": 50.8 * mm});
            skCircle(sketch, "E172", {"center": v(4549.52, 3772) * mm, "radius": 50.8 * mm});
            skLineSegment(sketch, "E173.0", {"start": v(5863.97, 3013.1) * mm, "end": v(4987.67, 3013.1) * mm});
            skLineSegment(sketch, "E173.1", {"start": v(4987.67, 3013.1) * mm, "end": v(4549.52, 3772) * mm});
            skLineSegment(sketch, "E173.2", {"start": v(4549.52, 3772) * mm, "end": v(4987.67, 4530.9) * mm});
            skLineSegment(sketch, "E173.3", {"start": v(4987.67, 4530.9) * mm, "end": v(5863.97, 4530.9) * mm});
            skLineSegment(sketch, "E173.4", {"start": v(5863.97, 4530.9) * mm, "end": v(6302.12, 3772) * mm});
            skLineSegment(sketch, "E173.5", {"start": v(6302.12, 3772) * mm, "end": v(5863.97, 3013.1) * mm});
            skPoint(sketch, "E173.0.midPoint", {"position": v(5425.82, 3013.1) * mm});
            skCircle(sketch, "E174", {"center": v(4987.67, 4530.9) * mm, "radius": 50.8 * mm});
            skCircle(sketch, "E175", {"center": v(5863.97, 3013.1) * mm, "radius": 50.8 * mm});
            skCircle(sketch, "E176", {"center": v(5863.97, 4530.9) * mm, "radius": 50.8 * mm});
            skCircle(sketch, "E177", {"center": v(6302.12, 3772) * mm, "radius": 50.8 * mm});
            skCircle(sketch, "E178", {"center": v(4987.67, 3013.1) * mm, "radius": 50.8 * mm});
            skCircle(sketch, "E179", {"center": v(4768.6, 3392.55) * mm, "radius": 25.4 * mm});
            skCircle(sketch, "E180", {"center": v(5425.82, 3013.1) * mm, "radius": 25.4 * mm});
            skCircle(sketch, "E181", {"center": v(6083.05, 3392.55) * mm, "radius": 25.4 * mm});
            skCircle(sketch, "E182", {"center": v(6083.05, 4151.45) * mm, "radius": 25.4 * mm});
            skCircle(sketch, "E183", {"center": v(5425.82, 4530.9) * mm, "radius": 25.4 * mm});
            skCircle(sketch, "E184", {"center": v(4768.6, 4151.45) * mm, "radius": 25.4 * mm});
            skFitSpline(sketch, "E185", {"points": [v(4987.67, 3063.9) * mm, v(5425.82, 3038.5) * mm, v(5863.97, 3063.9) * mm], "startDerivative": vector(876.3, -76.2) * mm, "endDerivative": vector(876.3, 76.2) * mm});
            skFitSpline(sketch, "E186", {"points": [v(4987.67, 2962.3) * mm, v(5425.82, 2987.7) * mm, v(5863.97, 2962.3) * mm], "startDerivative": vector(876.3, 76.2) * mm, "endDerivative": vector(876.3, -76.2) * mm});
            skCircle(sketch, "E187", {"center": v(4987.67, 3013.1) * mm, "radius": 12.7 * mm});
            skFitSpline(sketch, "E188", {"points": [v(4593.51, 3797.4) * mm, v(4790.6, 3405.25) * mm, v(5031.66, 3038.5) * mm], "startDerivative": vector(372.16, -797) * mm, "endDerivative": vector(504.14, -720.8) * mm});
            skFitSpline(sketch, "E189", {"points": [v(4505.53, 3746.6) * mm, v(4746.6, 3379.85) * mm, v(4943.68, 2987.7) * mm], "startDerivative": vector(504.14, -720.8) * mm, "endDerivative": vector(372.16, -797) * mm});
            skCircle(sketch, "E190", {"center": v(4549.52, 3772) * mm, "radius": 12.7 * mm});
            skFitSpline(sketch, "E191", {"points": [v(5819.98, 3038.5) * mm, v(6061.05, 3405.25) * mm, v(6258.13, 3797.4) * mm], "startDerivative": vector(504.14, 720.8) * mm, "endDerivative": vector(372.16, 797) * mm});
            skFitSpline(sketch, "E192", {"points": [v(5907.96, 2987.7) * mm, v(6105.04, 3379.85) * mm, v(6346.11, 3746.6) * mm], "startDerivative": vector(372.16, 797) * mm, "endDerivative": vector(504.14, 720.8) * mm});
            skCircle(sketch, "E193", {"center": v(5863.97, 3013.1) * mm, "radius": 12.7 * mm});
            skFitSpline(sketch, "E194", {"points": [v(6258.13, 3746.6) * mm, v(6061.05, 4138.75) * mm, v(5819.98, 4505.5) * mm], "startDerivative": vector(-372.16, 797) * mm, "endDerivative": vector(-504.14, 720.8) * mm});
            skFitSpline(sketch, "E195", {"points": [v(6346.11, 3797.4) * mm, v(6105.04, 4164.15) * mm, v(5907.96, 4556.3) * mm], "startDerivative": vector(-504.14, 720.8) * mm, "endDerivative": vector(-372.16, 797) * mm});
            skCircle(sketch, "E196", {"center": v(6302.12, 3772) * mm, "radius": 12.7 * mm});
            skFitSpline(sketch, "E197", {"points": [v(5031.66, 4505.5) * mm, v(4790.6, 4138.75) * mm, v(4593.51, 3746.6) * mm], "startDerivative": vector(-504.14, -720.8) * mm, "endDerivative": vector(-372.16, -797) * mm});
            skFitSpline(sketch, "E198", {"points": [v(4943.68, 4556.3) * mm, v(4746.6, 4164.15) * mm, v(4505.53, 3797.4) * mm], "startDerivative": vector(-372.16, -797) * mm, "endDerivative": vector(-504.14, -720.8) * mm});
            skCircle(sketch, "E199", {"center": v(4987.67, 4530.9) * mm, "radius": 12.7 * mm});
            skFitSpline(sketch, "E200", {"points": [v(5863.97, 4480.1) * mm, v(5425.82, 4505.5) * mm, v(4987.67, 4480.1) * mm], "startDerivative": vector(-876.3, 76.2) * mm, "endDerivative": vector(-876.3, -76.2) * mm});
            skFitSpline(sketch, "E201", {"points": [v(5863.97, 4581.7) * mm, v(5425.82, 4556.3) * mm, v(4987.67, 4581.7) * mm], "startDerivative": vector(-876.3, -76.2) * mm, "endDerivative": vector(-876.3, 76.2) * mm});
            skCircle(sketch, "E202", {"center": v(5863.97, 4530.9) * mm, "radius": 12.7 * mm});
            skLineSegment(sketch, "E203", {"start": v(5863.97, 4530.9) * mm, "end": v(5863.97, 3773.47) * mm, "construction": true});
            skLineSegment(sketch, "E204", {"start": v(5526.4, 3495.7) * mm, "end": v(4803.17, 3495.7) * mm});
            skLineSegment(sketch, "E205", {"start": v(6194, 3772) * mm, "end": v(5429.65, 3772) * mm});
            skLineSegment(sketch, "E206.right", {"start": v(3141.63, 3772) * mm, "end": v(3141.63, 2959.2) * mm, "construction": true});
            skLineSegment(sketch, "E207.5", {"start": v(2358.77, 4530.9) * mm, "end": v(1920.62, 3772) * mm});
            skCircle(sketch, "E208", {"center": v(1920.62, 3772) * mm, "radius": 50.8 * mm});
            skLineSegment(sketch, "E209.0", {"start": v(3235.07, 3013.1) * mm, "end": v(2358.77, 3013.1) * mm});
            skLineSegment(sketch, "E209.1", {"start": v(2358.77, 3013.1) * mm, "end": v(1920.62, 3772) * mm});
            skLineSegment(sketch, "E209.2", {"start": v(1920.62, 3772) * mm, "end": v(2358.77, 4530.9) * mm});
            skLineSegment(sketch, "E209.3", {"start": v(2358.77, 4530.9) * mm, "end": v(3235.07, 4530.9) * mm});
            skLineSegment(sketch, "E209.4", {"start": v(3235.07, 4530.9) * mm, "end": v(3673.22, 3772) * mm});
            skLineSegment(sketch, "E209.5", {"start": v(3673.22, 3772) * mm, "end": v(3235.07, 3013.1) * mm});
            skPoint(sketch, "E209.0.midPoint", {"position": v(2796.92, 3013.1) * mm});
            skCircle(sketch, "E210", {"center": v(2358.77, 4530.9) * mm, "radius": 50.8 * mm});
            skCircle(sketch, "E211", {"center": v(3235.07, 3013.1) * mm, "radius": 50.8 * mm});
            skCircle(sketch, "E212", {"center": v(3235.07, 4530.9) * mm, "radius": 50.8 * mm});
            skCircle(sketch, "E213", {"center": v(3673.22, 3772) * mm, "radius": 50.8 * mm});
            skCircle(sketch, "E214", {"center": v(2358.77, 3013.1) * mm, "radius": 50.8 * mm});
            skCircle(sketch, "E215", {"center": v(2139.7, 3392.55) * mm, "radius": 25.4 * mm});
            skCircle(sketch, "E216", {"center": v(2796.92, 3013.1) * mm, "radius": 25.4 * mm});
            skCircle(sketch, "E217", {"center": v(3454.15, 3392.55) * mm, "radius": 25.4 * mm});
            skCircle(sketch, "E218", {"center": v(3454.15, 4151.45) * mm, "radius": 25.4 * mm});
            skCircle(sketch, "E219", {"center": v(2796.92, 4530.9) * mm, "radius": 25.4 * mm});
            skCircle(sketch, "E220", {"center": v(2139.7, 4151.45) * mm, "radius": 25.4 * mm});
            skFitSpline(sketch, "E221", {"points": [v(2358.77, 3063.9) * mm, v(2796.92, 3038.5) * mm, v(3235.07, 3063.9) * mm], "startDerivative": vector(876.3, -76.2) * mm, "endDerivative": vector(876.3, 76.2) * mm});
            skFitSpline(sketch, "E222", {"points": [v(2358.77, 2962.3) * mm, v(2796.92, 2987.7) * mm, v(3235.07, 2962.3) * mm], "startDerivative": vector(876.3, 76.2) * mm, "endDerivative": vector(876.3, -76.2) * mm});
            skCircle(sketch, "E223", {"center": v(2358.77, 3013.1) * mm, "radius": 12.7 * mm});
            skFitSpline(sketch, "E224", {"points": [v(1964.61, 3797.4) * mm, v(2161.7, 3405.25) * mm, v(2402.76, 3038.5) * mm], "startDerivative": vector(372.16, -797) * mm, "endDerivative": vector(504.14, -720.8) * mm});
            skFitSpline(sketch, "E225", {"points": [v(1876.63, 3746.6) * mm, v(2117.7, 3379.85) * mm, v(2314.78, 2987.7) * mm], "startDerivative": vector(504.14, -720.8) * mm, "endDerivative": vector(372.16, -797) * mm});
            skCircle(sketch, "E226", {"center": v(1920.62, 3772) * mm, "radius": 12.7 * mm});
            skFitSpline(sketch, "E227", {"points": [v(3191.08, 3038.5) * mm, v(3432.15, 3405.25) * mm, v(3629.23, 3797.4) * mm], "startDerivative": vector(504.14, 720.8) * mm, "endDerivative": vector(372.16, 797) * mm});
            skFitSpline(sketch, "E228", {"points": [v(3279.06, 2987.7) * mm, v(3476.14, 3379.85) * mm, v(3717.21, 3746.6) * mm], "startDerivative": vector(372.16, 797) * mm, "endDerivative": vector(504.14, 720.8) * mm});
            skCircle(sketch, "E229", {"center": v(3235.07, 3013.1) * mm, "radius": 12.7 * mm});
            skFitSpline(sketch, "E230", {"points": [v(3629.23, 3746.6) * mm, v(3432.15, 4138.75) * mm, v(3191.08, 4505.5) * mm], "startDerivative": vector(-372.16, 797) * mm, "endDerivative": vector(-504.14, 720.8) * mm});
            skFitSpline(sketch, "E231", {"points": [v(3717.21, 3797.4) * mm, v(3476.14, 4164.15) * mm, v(3279.06, 4556.3) * mm], "startDerivative": vector(-504.14, 720.8) * mm, "endDerivative": vector(-372.16, 797) * mm});
            skCircle(sketch, "E232", {"center": v(3673.22, 3772) * mm, "radius": 12.7 * mm});
            skFitSpline(sketch, "E233", {"points": [v(2402.76, 4505.5) * mm, v(2161.7, 4138.75) * mm, v(1964.61, 3746.6) * mm], "startDerivative": vector(-504.14, -720.8) * mm, "endDerivative": vector(-372.16, -797) * mm});
            skFitSpline(sketch, "E234", {"points": [v(2314.78, 4556.3) * mm, v(2117.7, 4164.15) * mm, v(1876.63, 3797.4) * mm], "startDerivative": vector(-372.16, -797) * mm, "endDerivative": vector(-504.14, -720.8) * mm});
            skCircle(sketch, "E235", {"center": v(2358.77, 4530.9) * mm, "radius": 12.7 * mm});
            skFitSpline(sketch, "E236", {"points": [v(3235.07, 4480.1) * mm, v(2796.92, 4505.5) * mm, v(2358.77, 4480.1) * mm], "startDerivative": vector(-876.3, 76.2) * mm, "endDerivative": vector(-876.3, -76.2) * mm});
            skFitSpline(sketch, "E237", {"points": [v(3235.07, 4581.7) * mm, v(2796.92, 4556.3) * mm, v(2358.77, 4581.7) * mm], "startDerivative": vector(-876.3, -76.2) * mm, "endDerivative": vector(-876.3, 76.2) * mm});
            skCircle(sketch, "E238", {"center": v(3235.07, 4530.9) * mm, "radius": 12.7 * mm});
            skLineSegment(sketch, "E239", {"start": v(3235.07, 4530.9) * mm, "end": v(3235.07, 3773.47) * mm, "construction": true});
            skLineSegment(sketch, "E240", {"start": v(2897.5, 3495.7) * mm, "end": v(2174.27, 3495.7) * mm});
            skLineSegment(sketch, "E241", {"start": v(3565.1, 3772) * mm, "end": v(2800.75, 3772) * mm});
            skSolve(sketch);
        }
        {
            var Q0;
            Q0=makeQuery(id+"F0.imprint","IMPRINT",FACE,{"disambiguationData":[TD([[makeQuery(id+"F0.imprint","IMPRINT",EDGE,{"derivedFrom":sQuery(id+"F0.wireOp",EDGE,"E29")}),-1.0]])]});
            var Q1;
            Q1=makeQuery(id+"F0.imprint","IMPRINT",FACE,{"disambiguationData":[TD([[makeQuery(id+"F0.imprint","IMPRINT",EDGE,{"derivedFrom":sQuery(id+"F0.wireOp",EDGE,"E30")}),-1.0]])]});
            var Q2;
            Q2=makeQuery(id+"F0.imprint","IMPRINT",FACE,{"disambiguationData":[TD([[makeQuery(id+"F0.imprint","IMPRINT",EDGE,{"derivedFrom":sQuery(id+"F0.wireOp",EDGE,"E28")}),-1.0]])]});
            extrude(context, id + "F2", {"entities" : qUnion([Q0, Q1, Q2]), "depth" : 6.35 * mm});
        }
        {
            var Q0;
            Q0=makeQuery(id+"F2.opExtrude","SWEPT_BODY",BODY,{"disambiguationData":[OSD([sQuery(id+"F0.wireOp",EDGE,"E23"),sQuery(id+"F0.wireOp",EDGE,"E25"),sQuery(id+"F0.wireOp",EDGE,"E26"),sQuery(id+"F0.wireOp",EDGE,"E27"),sQuery(id+"F0.wireOp",EDGE,"E28"),sQuery(id+"F0.wireOp",EDGE,"E29"),sQuery(id+"F0.wireOp",EDGE,"E30"),sQuery(id+"F0.wireOp",EDGE,"E31.1.0.0"),sQuery(id+"F0.wireOp",EDGE,"E31.2.0.0"),sQuery(id+"F0.wireOp",EDGE,"E32.1.0.0"),sQuery(id+"F0.wireOp",EDGE,"E32.2.0.0"),sQuery(id+"F0.wireOp",EDGE,"E33"),sQuery(id+"F0.wireOp",EDGE,"E34"),sQuery(id+"F0.wireOp",EDGE,"E35.MirrorC"),sQuery(id+"F0.wireOp",EDGE,"E37.MirrorC")])]});
            var Q1;
            Q1=qCreatedBy(makeId("Origin.pointOp"),VERTEX);
            transform(context, id + "F3", {"entities" : qUnion([Q0]), "transformType" : TransformType.SCALE_UNIFORMLY, "scale" : 2, "scalePoint" : qUnion([Q1]), "makeCopy" : true});
        }
        {
            var Q0;
            Q0=makeQuery(id+"F3.opPattern","COPY",BODY,{"derivedFrom":makeQuery(id+"F2.opExtrude","SWEPT_BODY",BODY,{"disambiguationData":[OSD([sQuery(id+"F0.wireOp",EDGE,"E23"),sQuery(id+"F0.wireOp",EDGE,"E25"),sQuery(id+"F0.wireOp",EDGE,"E26"),sQuery(id+"F0.wireOp",EDGE,"E27"),sQuery(id+"F0.wireOp",EDGE,"E28"),sQuery(id+"F0.wireOp",EDGE,"E29"),sQuery(id+"F0.wireOp",EDGE,"E30"),sQuery(id+"F0.wireOp",EDGE,"E31.1.0.0"),sQuery(id+"F0.wireOp",EDGE,"E31.2.0.0"),sQuery(id+"F0.wireOp",EDGE,"E32.1.0.0"),sQuery(id+"F0.wireOp",EDGE,"E32.2.0.0"),sQuery(id+"F0.wireOp",EDGE,"E33"),sQuery(id+"F0.wireOp",EDGE,"E34"),sQuery(id+"F0.wireOp",EDGE,"E35.MirrorC"),sQuery(id+"F0.wireOp",EDGE,"E37.MirrorC")])]}),"instanceName":"1"});
            var Q1;
            Q1=makeQuery(id+"F3.opPattern","COPY",EDGE,{"derivedFrom":makeQuery(id+"F2.opExtrude","CAP_EDGE",EDGE,{"disambiguationData":[OSD([sQuery(id+"F0.wireOp",EDGE,"E29")])],"isStart":true}),"instanceName":"1"});
            transform(context, id + "F4", {"entities" : qUnion([Q0]), "transformType" : TransformType.ROTATION, "transformAxis" : qUnion([Q1]), "angle" : 120 * degree, "makeCopy" : true});
        }
        {
            var Q0;
            Q0=makeQuery(id+"F4.opPattern","COPY",BODY,{"derivedFrom":makeQuery(id+"F3.opPattern","COPY",BODY,{"derivedFrom":makeQuery(id+"F2.opExtrude","SWEPT_BODY",BODY,{"disambiguationData":[OSD([sQuery(id+"F0.wireOp",EDGE,"E23"),sQuery(id+"F0.wireOp",EDGE,"E25"),sQuery(id+"F0.wireOp",EDGE,"E26"),sQuery(id+"F0.wireOp",EDGE,"E27"),sQuery(id+"F0.wireOp",EDGE,"E28"),sQuery(id+"F0.wireOp",EDGE,"E29"),sQuery(id+"F0.wireOp",EDGE,"E30"),sQuery(id+"F0.wireOp",EDGE,"E31.1.0.0"),sQuery(id+"F0.wireOp",EDGE,"E31.2.0.0"),sQuery(id+"F0.wireOp",EDGE,"E32.1.0.0"),sQuery(id+"F0.wireOp",EDGE,"E32.2.0.0"),sQuery(id+"F0.wireOp",EDGE,"E33"),sQuery(id+"F0.wireOp",EDGE,"E34"),sQuery(id+"F0.wireOp",EDGE,"E35.MirrorC"),sQuery(id+"F0.wireOp",EDGE,"E37.MirrorC")])]}),"instanceName":"1"}),"instanceName":"1"});
            var Q1;
            Q1=makeQuery(id+"F3.opPattern","COPY",EDGE,{"derivedFrom":makeQuery(id+"F2.opExtrude","CAP_EDGE",EDGE,{"disambiguationData":[OSD([sQuery(id+"F0.wireOp",EDGE,"E29")])],"isStart":false}),"instanceName":"1"});
            transform(context, id + "F5", {"entities" : qUnion([Q0]), "transformType" : TransformType.ROTATION, "transformAxis" : qUnion([Q1]), "angle" : 120 * degree, "makeCopy" : true});
        }
        {
            var Q0;
            Q0=makeQuery(id+"F3.opPattern","COPY",BODY,{"derivedFrom":makeQuery(id+"F2.opExtrude","SWEPT_BODY",BODY,{"disambiguationData":[OSD([sQuery(id+"F0.wireOp",EDGE,"E23"),sQuery(id+"F0.wireOp",EDGE,"E25"),sQuery(id+"F0.wireOp",EDGE,"E26"),sQuery(id+"F0.wireOp",EDGE,"E27"),sQuery(id+"F0.wireOp",EDGE,"E28"),sQuery(id+"F0.wireOp",EDGE,"E29"),sQuery(id+"F0.wireOp",EDGE,"E30"),sQuery(id+"F0.wireOp",EDGE,"E31.1.0.0"),sQuery(id+"F0.wireOp",EDGE,"E31.2.0.0"),sQuery(id+"F0.wireOp",EDGE,"E32.1.0.0"),sQuery(id+"F0.wireOp",EDGE,"E32.2.0.0"),sQuery(id+"F0.wireOp",EDGE,"E33"),sQuery(id+"F0.wireOp",EDGE,"E34"),sQuery(id+"F0.wireOp",EDGE,"E35.MirrorC"),sQuery(id+"F0.wireOp",EDGE,"E37.MirrorC")])]}),"instanceName":"1"});
            var Q1;
            Q1=makeQuery(id+"F3.opPattern","COPY",EDGE,{"derivedFrom":makeQuery(id+"F2.opExtrude","CAP_EDGE",EDGE,{"disambiguationData":[OSD([sQuery(id+"F0.wireOp",EDGE,"E28")])],"isStart":false}),"instanceName":"1"});
            transform(context, id + "F6", {"entities" : qUnion([Q0]), "transformType" : TransformType.ROTATION, "transformAxis" : qUnion([Q1]), "angle" : 120 * degree, "makeCopy" : true});
        }
        {
            var Q0;
            Q0=makeQuery(id+"F6.opPattern","COPY",BODY,{"derivedFrom":makeQuery(id+"F3.opPattern","COPY",BODY,{"derivedFrom":makeQuery(id+"F2.opExtrude","SWEPT_BODY",BODY,{"disambiguationData":[OSD([sQuery(id+"F0.wireOp",EDGE,"E23"),sQuery(id+"F0.wireOp",EDGE,"E25"),sQuery(id+"F0.wireOp",EDGE,"E26"),sQuery(id+"F0.wireOp",EDGE,"E27"),sQuery(id+"F0.wireOp",EDGE,"E28"),sQuery(id+"F0.wireOp",EDGE,"E29"),sQuery(id+"F0.wireOp",EDGE,"E30"),sQuery(id+"F0.wireOp",EDGE,"E31.1.0.0"),sQuery(id+"F0.wireOp",EDGE,"E31.2.0.0"),sQuery(id+"F0.wireOp",EDGE,"E32.1.0.0"),sQuery(id+"F0.wireOp",EDGE,"E32.2.0.0"),sQuery(id+"F0.wireOp",EDGE,"E33"),sQuery(id+"F0.wireOp",EDGE,"E34"),sQuery(id+"F0.wireOp",EDGE,"E35.MirrorC"),sQuery(id+"F0.wireOp",EDGE,"E37.MirrorC")])]}),"instanceName":"1"}),"instanceName":"1"});
            var Q1;
            Q1=makeQuery(id+"F6.opPattern","COPY",EDGE,{"derivedFrom":makeQuery(id+"F3.opPattern","COPY",EDGE,{"derivedFrom":makeQuery(id+"F2.opExtrude","CAP_EDGE",EDGE,{"disambiguationData":[OSD([sQuery(id+"F0.wireOp",EDGE,"E29")])],"isStart":false}),"instanceName":"1"}),"instanceName":"1"});
            transform(context, id + "F7", {"entities" : qUnion([Q0]), "transformType" : TransformType.ROTATION, "transformAxis" : qUnion([Q1]), "angle" : 120 * degree, "oppositeDirection" : true, "makeCopy" : true});
        }
        {
            var Q0;
            Q0=makeQuery(id+"F7.opPattern","COPY",BODY,{"derivedFrom":makeQuery(id+"F6.opPattern","COPY",BODY,{"derivedFrom":makeQuery(id+"F3.opPattern","COPY",BODY,{"derivedFrom":makeQuery(id+"F2.opExtrude","SWEPT_BODY",BODY,{"disambiguationData":[OSD([sQuery(id+"F0.wireOp",EDGE,"E23"),sQuery(id+"F0.wireOp",EDGE,"E25"),sQuery(id+"F0.wireOp",EDGE,"E26"),sQuery(id+"F0.wireOp",EDGE,"E27"),sQuery(id+"F0.wireOp",EDGE,"E28"),sQuery(id+"F0.wireOp",EDGE,"E29"),sQuery(id+"F0.wireOp",EDGE,"E30"),sQuery(id+"F0.wireOp",EDGE,"E31.1.0.0"),sQuery(id+"F0.wireOp",EDGE,"E31.2.0.0"),sQuery(id+"F0.wireOp",EDGE,"E32.1.0.0"),sQuery(id+"F0.wireOp",EDGE,"E32.2.0.0"),sQuery(id+"F0.wireOp",EDGE,"E33"),sQuery(id+"F0.wireOp",EDGE,"E34"),sQuery(id+"F0.wireOp",EDGE,"E35.MirrorC"),sQuery(id+"F0.wireOp",EDGE,"E37.MirrorC")])]}),"instanceName":"1"}),"instanceName":"1"}),"instanceName":"1"});
            var Q1;
            Q1=makeQuery(id+"F7.opPattern","COPY",EDGE,{"derivedFrom":makeQuery(id+"F6.opPattern","COPY",EDGE,{"derivedFrom":makeQuery(id+"F3.opPattern","COPY",EDGE,{"derivedFrom":makeQuery(id+"F2.opExtrude","CAP_EDGE",EDGE,{"disambiguationData":[OSD([sQuery(id+"F0.wireOp",EDGE,"E28")])],"isStart":false}),"instanceName":"1"}),"instanceName":"1"}),"instanceName":"1"});
            transform(context, id + "F8", {"entities" : qUnion([Q0]), "transformType" : TransformType.ROTATION, "transformAxis" : qUnion([Q1]), "angle" : 120 * degree, "oppositeDirection" : true, "makeCopy" : true});
        }
        {
            var Q0;
            {var subQ0=sQuery(id+"F1.wireOp",EDGE,"E174");var subQ1=sQuery(id+"F1.wireOp",EDGE,"E173.3");var subQ2=makeQuery(id+"F1.imprint","INTERSECT",VERTEX,{"derivedFrom":[subQ1,subQ0]});Q0=makeQuery(id+"F1.imprint","IMPRINT",FACE,{"disambiguationData":[TD([[makeQuery(id+"F1.imprint","IMPRINT",EDGE,{"disambiguationData":[TD([[subQ2,-1.0]])],"derivedFrom":subQ1}),1.0]])]});}
            var Q1;
            {var subQ1=sQuery(id+"F1.wireOp",EDGE,"E174");var subQ3=sQuery(id+"F1.wireOp",EDGE,"E173.3");var subQ4=makeQuery(id+"F1.imprint","INTERSECT",VERTEX,{"derivedFrom":[subQ3,subQ1]});Q1=makeQuery(id+"F1.imprint","IMPRINT",FACE,{"disambiguationData":[TD([[makeQuery(id+"F1.imprint","IMPRINT",EDGE,{"disambiguationData":[TD([[subQ4,-1.0]])],"derivedFrom":subQ3}),-1.0]])]});}
            var Q2;
            {var subQ1=sQuery(id+"F1.wireOp",EDGE,"E174");var subQ3=sQuery(id+"F1.wireOp",EDGE,"E169.4");var subQ4=makeQuery(id+"F1.imprint","INTERSECT",VERTEX,{"derivedFrom":[subQ3,subQ1]});Q2=makeQuery(id+"F1.imprint","IMPRINT",FACE,{"disambiguationData":[TD([[makeQuery(id+"F1.imprint","IMPRINT",EDGE,{"disambiguationData":[TD([[subQ4,-1.0]])],"derivedFrom":subQ3}),1.0]])]});}
            var Q3;
            {var subQ1=sQuery(id+"F1.wireOp",EDGE,"E174");var subQ6=sQuery(id+"F1.wireOp",EDGE,"E173.2");var subQ7=makeQuery(id+"F1.imprint","INTERSECT",VERTEX,{"derivedFrom":[subQ6,subQ1]});Q3=makeQuery(id+"F1.imprint","IMPRINT",FACE,{"disambiguationData":[TD([[makeQuery(id+"F1.imprint","IMPRINT",EDGE,{"disambiguationData":[TD([[subQ7,-1.0]])],"derivedFrom":subQ6}),-1.0]])]});}
            var Q4;
            {var subQ0=sQuery(id+"F1.wireOp",EDGE,"E174");var subQ8=sQuery(id+"F1.wireOp",EDGE,"E169.4");var subQ9=makeQuery(id+"F1.imprint","INTERSECT",VERTEX,{"derivedFrom":[subQ8,subQ0]});Q4=makeQuery(id+"F1.imprint","IMPRINT",FACE,{"disambiguationData":[TD([[makeQuery(id+"F1.imprint","IMPRINT",EDGE,{"disambiguationData":[TD([[subQ9,-1.0]])],"derivedFrom":subQ8}),-1.0]])]});}
            var Q5;
            {var subQ0=sQuery(id+"F1.wireOp",EDGE,"E184");var subQ1=sQuery(id+"F1.wireOp",EDGE,"E173.2");var subQ2=makeQuery(id+"F1.imprint","INTERSECT",VERTEX,{"disambiguationData":[OD(1.0)],"derivedFrom":[subQ1,subQ0]});Q5=makeQuery(id+"F1.imprint","IMPRINT",FACE,{"disambiguationData":[TD([[makeQuery(id+"F1.imprint","IMPRINT",EDGE,{"disambiguationData":[TD([[subQ2,-1.0]])],"derivedFrom":subQ1}),1.0]])]});}
            var Q6;
            {var subQ0=sQuery(id+"F1.wireOp",EDGE,"E184");var subQ1=sQuery(id+"F1.wireOp",EDGE,"E173.2");var subQ2=makeQuery(id+"F1.imprint","INTERSECT",VERTEX,{"disambiguationData":[OD(1.0)],"derivedFrom":[subQ1,subQ0]});Q6=makeQuery(id+"F1.imprint","IMPRINT",FACE,{"disambiguationData":[TD([[makeQuery(id+"F1.imprint","IMPRINT",EDGE,{"disambiguationData":[TD([[subQ2,-1.0]])],"derivedFrom":subQ1}),-1.0]])]});}
            var Q7;
            {var subQ0=sQuery(id+"F1.wireOp",EDGE,"E184");var subQ1=sQuery(id+"F1.wireOp",EDGE,"E173.2");var subQ2=makeQuery(id+"F1.imprint","INTERSECT",VERTEX,{"disambiguationData":[OD(0.0)],"derivedFrom":[subQ1,subQ0]});Q7=makeQuery(id+"F1.imprint","IMPRINT",FACE,{"disambiguationData":[TD([[makeQuery(id+"F1.imprint","IMPRINT",EDGE,{"disambiguationData":[TD([[subQ2,-1.0]])],"derivedFrom":subQ1}),-1.0]])]});}
            var Q8;
            {var subQ0=sQuery(id+"F1.wireOp",EDGE,"E184");var subQ1=sQuery(id+"F1.wireOp",EDGE,"E173.2");var subQ2=makeQuery(id+"F1.imprint","INTERSECT",VERTEX,{"disambiguationData":[OD(0.0)],"derivedFrom":[subQ1,subQ0]});Q8=makeQuery(id+"F1.imprint","IMPRINT",FACE,{"disambiguationData":[TD([[makeQuery(id+"F1.imprint","IMPRINT",EDGE,{"disambiguationData":[TD([[subQ2,-1.0]])],"derivedFrom":subQ1}),1.0]])]});}
            var Q9;
            {var subQ1=sQuery(id+"F1.wireOp",EDGE,"E172");var subQ7=sQuery(id+"F1.wireOp",EDGE,"E188");var subQ8=makeQuery(id+"F1.imprint","INTERSECT",VERTEX,{"disambiguationData":[OD(0.0)],"derivedFrom":[subQ1,subQ7]});Q9=makeQuery(id+"F1.imprint","IMPRINT",FACE,{"disambiguationData":[TD([[makeQuery(id+"F1.imprint","IMPRINT",EDGE,{"disambiguationData":[TD([[subQ8,1.0]])],"derivedFrom":subQ1}),-1.0]])]});}
            var Q10;
            {var subQ0=sQuery(id+"F1.wireOp",EDGE,"E173.2");var subQ1=sQuery(id+"F1.wireOp",EDGE,"E172");var subQ2=makeQuery(id+"F1.imprint","INTERSECT",VERTEX,{"derivedFrom":[subQ1,subQ0]});Q10=makeQuery(id+"F1.imprint","IMPRINT",FACE,{"disambiguationData":[TD([[makeQuery(id+"F1.imprint","IMPRINT",EDGE,{"disambiguationData":[TD([[subQ2,-1.0]])],"derivedFrom":subQ1}),-1.0]])]});}
            var Q11;
            {var subQ0=sQuery(id+"F1.wireOp",EDGE,"E188");var subQ1=sQuery(id+"F1.wireOp",EDGE,"E172");var subQ9=makeQuery(id+"F1.imprint","INTERSECT",VERTEX,{"disambiguationData":[OD(0.0)],"derivedFrom":[subQ1,subQ0]});Q11=makeQuery(id+"F1.imprint","IMPRINT",FACE,{"disambiguationData":[TD([[makeQuery(id+"F1.imprint","IMPRINT",EDGE,{"disambiguationData":[TD([[subQ9,-1.0]])],"derivedFrom":subQ1}),1.0]])]});}
            var Q12;
            {var subQ1=sQuery(id+"F1.wireOp",EDGE,"E172");var subQ7=sQuery(id+"F1.wireOp",EDGE,"E169.0");var subQ8=makeQuery(id+"F1.imprint","INTERSECT",VERTEX,{"derivedFrom":[subQ7,subQ1]});Q12=makeQuery(id+"F1.imprint","IMPRINT",FACE,{"disambiguationData":[TD([[makeQuery(id+"F1.imprint","IMPRINT",EDGE,{"disambiguationData":[TD([[subQ8,1.0]])],"derivedFrom":subQ7}),-1.0]])]});}
            var Q13;
            {var subQ1=sQuery(id+"F1.wireOp",EDGE,"E172");var subQ6=sQuery(id+"F1.wireOp",EDGE,"E169.0");var subQ7=makeQuery(id+"F1.imprint","INTERSECT",VERTEX,{"derivedFrom":[subQ6,subQ1]});Q13=makeQuery(id+"F1.imprint","IMPRINT",FACE,{"disambiguationData":[TD([[makeQuery(id+"F1.imprint","IMPRINT",EDGE,{"disambiguationData":[TD([[subQ7,1.0]])],"derivedFrom":subQ6}),1.0]])]});}
            var Q14;
            {var subQ0=sQuery(id+"F1.wireOp",EDGE,"E189");var subQ1=sQuery(id+"F1.wireOp",EDGE,"E172");var subQ2=makeQuery(id+"F1.imprint","INTERSECT",VERTEX,{"disambiguationData":[OD(1.0)],"derivedFrom":[subQ1,subQ0]});Q14=makeQuery(id+"F1.imprint","IMPRINT",FACE,{"disambiguationData":[TD([[makeQuery(id+"F1.imprint","IMPRINT",EDGE,{"disambiguationData":[TD([[subQ2,-1.0]])],"derivedFrom":subQ1}),-1.0]])]});}
            var Q15;
            {var subQ1=sQuery(id+"F1.wireOp",EDGE,"E172");var subQ7=sQuery(id+"F1.wireOp",EDGE,"E197");var subQ10=makeQuery(id+"F1.imprint","INTERSECT",VERTEX,{"disambiguationData":[OD(0.0)],"derivedFrom":[subQ1,subQ7]});Q15=makeQuery(id+"F1.imprint","IMPRINT",FACE,{"disambiguationData":[TD([[makeQuery(id+"F1.imprint","IMPRINT",EDGE,{"disambiguationData":[TD([[subQ10,1.0]])],"derivedFrom":subQ1}),-1.0]])]});}
            var Q16;
            {var subQ0=sQuery(id+"F1.wireOp",EDGE,"E188");var subQ1=sQuery(id+"F1.wireOp",EDGE,"E172");var subQ2=makeQuery(id+"F1.imprint","INTERSECT",VERTEX,{"disambiguationData":[OD(1.0)],"derivedFrom":[subQ1,subQ0]});Q16=makeQuery(id+"F1.imprint","IMPRINT",FACE,{"disambiguationData":[TD([[makeQuery(id+"F1.imprint","IMPRINT",EDGE,{"disambiguationData":[TD([[subQ2,1.0]])],"derivedFrom":subQ1}),-1.0]])]});}
            var Q17;
            {var subQ0=sQuery(id+"F1.wireOp",EDGE,"E179");var subQ1=sQuery(id+"F1.wireOp",EDGE,"E173.1");var subQ2=makeQuery(id+"F1.imprint","INTERSECT",VERTEX,{"disambiguationData":[OD(0.0)],"derivedFrom":[subQ1,subQ0]});Q17=makeQuery(id+"F1.imprint","IMPRINT",FACE,{"disambiguationData":[TD([[makeQuery(id+"F1.imprint","IMPRINT",EDGE,{"disambiguationData":[TD([[subQ2,-1.0]])],"derivedFrom":subQ1}),1.0]])]});}
            var Q18;
            {var subQ1=sQuery(id+"F1.wireOp",EDGE,"E178");var subQ3=sQuery(id+"F1.wireOp",EDGE,"E173.1");var subQ4=makeQuery(id+"F1.imprint","INTERSECT",VERTEX,{"derivedFrom":[subQ3,subQ1]});Q18=makeQuery(id+"F1.imprint","IMPRINT",FACE,{"disambiguationData":[TD([[makeQuery(id+"F1.imprint","IMPRINT",EDGE,{"disambiguationData":[TD([[subQ4,-1.0]])],"derivedFrom":subQ3}),-1.0]])]});}
            var Q19;
            {var subQ0=sQuery(id+"F1.wireOp",EDGE,"E179");var subQ1=sQuery(id+"F1.wireOp",EDGE,"E173.1");var subQ2=makeQuery(id+"F1.imprint","INTERSECT",VERTEX,{"disambiguationData":[OD(0.0)],"derivedFrom":[subQ1,subQ0]});Q19=makeQuery(id+"F1.imprint","IMPRINT",FACE,{"disambiguationData":[TD([[makeQuery(id+"F1.imprint","IMPRINT",EDGE,{"disambiguationData":[TD([[subQ2,-1.0]])],"derivedFrom":subQ1}),-1.0]])]});}
            var Q20;
            {var subQ0=sQuery(id+"F1.wireOp",EDGE,"E178");var subQ1=sQuery(id+"F1.wireOp",EDGE,"E173.1");var subQ2=makeQuery(id+"F1.imprint","INTERSECT",VERTEX,{"derivedFrom":[subQ1,subQ0]});Q20=makeQuery(id+"F1.imprint","IMPRINT",FACE,{"disambiguationData":[TD([[makeQuery(id+"F1.imprint","IMPRINT",EDGE,{"disambiguationData":[TD([[subQ2,-1.0]])],"derivedFrom":subQ1}),1.0]])]});}
            var Q21;
            {var subQ1=sQuery(id+"F1.wireOp",EDGE,"E178");var subQ11=sQuery(id+"F1.wireOp",EDGE,"E173.0");var subQ12=makeQuery(id+"F1.imprint","INTERSECT",VERTEX,{"derivedFrom":[subQ11,subQ1]});Q21=makeQuery(id+"F1.imprint","IMPRINT",FACE,{"disambiguationData":[TD([[makeQuery(id+"F1.imprint","IMPRINT",EDGE,{"disambiguationData":[TD([[subQ12,-1.0]])],"derivedFrom":subQ11}),1.0]])]});}
            var Q22;
            {var subQ0=sQuery(id+"F1.wireOp",EDGE,"E180");var subQ1=sQuery(id+"F1.wireOp",EDGE,"E173.0");var subQ2=makeQuery(id+"F1.imprint","INTERSECT",VERTEX,{"disambiguationData":[OD(1.0)],"derivedFrom":[subQ1,subQ0]});Q22=makeQuery(id+"F1.imprint","IMPRINT",FACE,{"disambiguationData":[TD([[makeQuery(id+"F1.imprint","IMPRINT",EDGE,{"disambiguationData":[TD([[subQ2,-1.0]])],"derivedFrom":subQ1}),1.0]])]});}
            var Q23;
            {var subQ0=sQuery(id+"F1.wireOp",EDGE,"E180");var subQ1=sQuery(id+"F1.wireOp",EDGE,"E173.0");var subQ2=makeQuery(id+"F1.imprint","INTERSECT",VERTEX,{"disambiguationData":[OD(1.0)],"derivedFrom":[subQ1,subQ0]});Q23=makeQuery(id+"F1.imprint","IMPRINT",FACE,{"disambiguationData":[TD([[makeQuery(id+"F1.imprint","IMPRINT",EDGE,{"disambiguationData":[TD([[subQ2,-1.0]])],"derivedFrom":subQ1}),-1.0]])]});}
            var Q24;
            {var subQ1=sQuery(id+"F1.wireOp",EDGE,"E178");var subQ3=sQuery(id+"F1.wireOp",EDGE,"E173.0");var subQ4=makeQuery(id+"F1.imprint","INTERSECT",VERTEX,{"derivedFrom":[subQ3,subQ1]});Q24=makeQuery(id+"F1.imprint","IMPRINT",FACE,{"disambiguationData":[TD([[makeQuery(id+"F1.imprint","IMPRINT",EDGE,{"disambiguationData":[TD([[subQ4,-1.0]])],"derivedFrom":subQ3}),-1.0]])]});}
            var Q25;
            {var subQ0=sQuery(id+"F1.wireOp",EDGE,"E188");var subQ1=sQuery(id+"F1.wireOp",EDGE,"E178");var subQ2=makeQuery(id+"F1.imprint","INTERSECT",VERTEX,{"disambiguationData":[OD(1.0)],"derivedFrom":[subQ1,subQ0]});Q25=makeQuery(id+"F1.imprint","IMPRINT",FACE,{"disambiguationData":[TD([[makeQuery(id+"F1.imprint","IMPRINT",EDGE,{"disambiguationData":[TD([[subQ2,-1.0]])],"derivedFrom":subQ1}),-1.0]])]});}
            var Q26;
            {var subQ0=sQuery(id+"F1.wireOp",EDGE,"E180");var subQ1=sQuery(id+"F1.wireOp",EDGE,"E173.0");var subQ2=makeQuery(id+"F1.imprint","INTERSECT",VERTEX,{"disambiguationData":[OD(0.0)],"derivedFrom":[subQ1,subQ0]});Q26=makeQuery(id+"F1.imprint","IMPRINT",FACE,{"disambiguationData":[TD([[makeQuery(id+"F1.imprint","IMPRINT",EDGE,{"disambiguationData":[TD([[subQ2,-1.0]])],"derivedFrom":subQ1}),-1.0]])]});}
            var Q27;
            {var subQ1=sQuery(id+"F1.wireOp",EDGE,"E175");var subQ5=sQuery(id+"F1.wireOp",EDGE,"E173.0");var subQ9=makeQuery(id+"F1.imprint","INTERSECT",VERTEX,{"derivedFrom":[subQ5,subQ1]});Q27=makeQuery(id+"F1.imprint","IMPRINT",FACE,{"disambiguationData":[TD([[makeQuery(id+"F1.imprint","IMPRINT",EDGE,{"disambiguationData":[TD([[subQ9,-1.0]])],"derivedFrom":subQ5}),-1.0]])]});}
            var Q28;
            {var subQ0=sQuery(id+"F1.wireOp",EDGE,"E180");var subQ1=sQuery(id+"F1.wireOp",EDGE,"E173.0");var subQ2=makeQuery(id+"F1.imprint","INTERSECT",VERTEX,{"disambiguationData":[OD(0.0)],"derivedFrom":[subQ1,subQ0]});Q28=makeQuery(id+"F1.imprint","IMPRINT",FACE,{"disambiguationData":[TD([[makeQuery(id+"F1.imprint","IMPRINT",EDGE,{"disambiguationData":[TD([[subQ2,-1.0]])],"derivedFrom":subQ1}),1.0]])]});}
            var Q29;
            {var subQ0=sQuery(id+"F1.wireOp",EDGE,"E175");var subQ1=sQuery(id+"F1.wireOp",EDGE,"E173.0");var subQ2=makeQuery(id+"F1.imprint","INTERSECT",VERTEX,{"derivedFrom":[subQ1,subQ0]});Q29=makeQuery(id+"F1.imprint","IMPRINT",FACE,{"disambiguationData":[TD([[makeQuery(id+"F1.imprint","IMPRINT",EDGE,{"disambiguationData":[TD([[subQ2,-1.0]])],"derivedFrom":subQ1}),1.0]])]});}
            var Q30;
            {var subQ3=sQuery(id+"F1.wireOp",EDGE,"E173.0");var subQ11=sQuery(id+"F1.wireOp",EDGE,"E193");var subQ13=makeQuery(id+"F1.imprint","INTERSECT",VERTEX,{"derivedFrom":[subQ3,subQ11]});Q30=makeQuery(id+"F1.imprint","IMPRINT",FACE,{"disambiguationData":[TD([[makeQuery(id+"F1.imprint","IMPRINT",EDGE,{"disambiguationData":[TD([[subQ13,-1.0]])],"derivedFrom":subQ3}),1.0]])]});}
            var Q31;
            {var subQ0=sQuery(id+"F1.wireOp",EDGE,"E181");var subQ1=sQuery(id+"F1.wireOp",EDGE,"E173.5");var subQ2=makeQuery(id+"F1.imprint","INTERSECT",VERTEX,{"disambiguationData":[OD(1.0)],"derivedFrom":[subQ1,subQ0]});Q31=makeQuery(id+"F1.imprint","IMPRINT",FACE,{"disambiguationData":[TD([[makeQuery(id+"F1.imprint","IMPRINT",EDGE,{"disambiguationData":[TD([[subQ2,-1.0]])],"derivedFrom":subQ1}),1.0]])]});}
            var Q32;
            {var subQ5=sQuery(id+"F1.wireOp",EDGE,"E193");var subQ6=sQuery(id+"F1.wireOp",EDGE,"E173.0");var subQ7=makeQuery(id+"F1.imprint","INTERSECT",VERTEX,{"derivedFrom":[subQ6,subQ5]});Q32=makeQuery(id+"F1.imprint","IMPRINT",FACE,{"disambiguationData":[TD([[makeQuery(id+"F1.imprint","IMPRINT",EDGE,{"disambiguationData":[TD([[subQ7,-1.0]])],"derivedFrom":subQ6}),-1.0]])]});}
            var Q33;
            {var subQ0=sQuery(id+"F1.wireOp",EDGE,"E181");var subQ1=sQuery(id+"F1.wireOp",EDGE,"E173.5");var subQ2=makeQuery(id+"F1.imprint","INTERSECT",VERTEX,{"disambiguationData":[OD(1.0)],"derivedFrom":[subQ1,subQ0]});Q33=makeQuery(id+"F1.imprint","IMPRINT",FACE,{"disambiguationData":[TD([[makeQuery(id+"F1.imprint","IMPRINT",EDGE,{"disambiguationData":[TD([[subQ2,-1.0]])],"derivedFrom":subQ1}),-1.0]])]});}
            var Q34;
            {var subQ0=sQuery(id+"F1.wireOp",EDGE,"E185");var subQ1=sQuery(id+"F1.wireOp",EDGE,"E175");var subQ2=makeQuery(id+"F1.imprint","INTERSECT",VERTEX,{"disambiguationData":[OD(1.0)],"derivedFrom":[subQ1,subQ0]});Q34=makeQuery(id+"F1.imprint","IMPRINT",FACE,{"disambiguationData":[TD([[makeQuery(id+"F1.imprint","IMPRINT",EDGE,{"disambiguationData":[TD([[subQ2,-1.0]])],"derivedFrom":subQ1}),-1.0]])]});}
            var Q35;
            {var subQ0=sQuery(id+"F1.wireOp",EDGE,"E181");var subQ1=sQuery(id+"F1.wireOp",EDGE,"E173.5");var subQ2=makeQuery(id+"F1.imprint","INTERSECT",VERTEX,{"disambiguationData":[OD(0.0)],"derivedFrom":[subQ1,subQ0]});Q35=makeQuery(id+"F1.imprint","IMPRINT",FACE,{"disambiguationData":[TD([[makeQuery(id+"F1.imprint","IMPRINT",EDGE,{"disambiguationData":[TD([[subQ2,-1.0]])],"derivedFrom":subQ1}),1.0]])]});}
            var Q36;
            {var subQ0=sQuery(id+"F1.wireOp",EDGE,"E181");var subQ1=sQuery(id+"F1.wireOp",EDGE,"E173.5");var subQ2=makeQuery(id+"F1.imprint","INTERSECT",VERTEX,{"disambiguationData":[OD(0.0)],"derivedFrom":[subQ1,subQ0]});Q36=makeQuery(id+"F1.imprint","IMPRINT",FACE,{"disambiguationData":[TD([[makeQuery(id+"F1.imprint","IMPRINT",EDGE,{"disambiguationData":[TD([[subQ2,-1.0]])],"derivedFrom":subQ1}),-1.0]])]});}
            var Q37;
            {var subQ1=sQuery(id+"F1.wireOp",EDGE,"E173.5");var subQ6=sQuery(id+"F1.wireOp",EDGE,"E177");var subQ8=makeQuery(id+"F1.imprint","INTERSECT",VERTEX,{"derivedFrom":[subQ1,subQ6]});Q37=makeQuery(id+"F1.imprint","IMPRINT",FACE,{"disambiguationData":[TD([[makeQuery(id+"F1.imprint","IMPRINT",EDGE,{"disambiguationData":[TD([[subQ8,-1.0]])],"derivedFrom":subQ1}),-1.0]])]});}
            var Q38;
            {var subQ0=sQuery(id+"F1.wireOp",EDGE,"E177");var subQ1=sQuery(id+"F1.wireOp",EDGE,"E173.5");var subQ2=makeQuery(id+"F1.imprint","INTERSECT",VERTEX,{"derivedFrom":[subQ1,subQ0]});Q38=makeQuery(id+"F1.imprint","IMPRINT",FACE,{"disambiguationData":[TD([[makeQuery(id+"F1.imprint","IMPRINT",EDGE,{"disambiguationData":[TD([[subQ2,-1.0]])],"derivedFrom":subQ1}),1.0]])]});}
            var Q39;
            {var subQ0=sQuery(id+"F1.wireOp",EDGE,"E182");var subQ1=sQuery(id+"F1.wireOp",EDGE,"E173.4");var subQ2=makeQuery(id+"F1.imprint","INTERSECT",VERTEX,{"disambiguationData":[OD(1.0)],"derivedFrom":[subQ1,subQ0]});Q39=makeQuery(id+"F1.imprint","IMPRINT",FACE,{"disambiguationData":[TD([[makeQuery(id+"F1.imprint","IMPRINT",EDGE,{"disambiguationData":[TD([[subQ2,-1.0]])],"derivedFrom":subQ1}),1.0]])]});}
            var Q40;
            {var subQ4=sQuery(id+"F1.wireOp",EDGE,"E182");var subQ5=sQuery(id+"F1.wireOp",EDGE,"E173.4");var subQ6=makeQuery(id+"F1.imprint","INTERSECT",VERTEX,{"disambiguationData":[OD(1.0)],"derivedFrom":[subQ5,subQ4]});Q40=makeQuery(id+"F1.imprint","IMPRINT",FACE,{"disambiguationData":[TD([[makeQuery(id+"F1.imprint","IMPRINT",EDGE,{"disambiguationData":[TD([[subQ6,-1.0]])],"derivedFrom":subQ5}),-1.0]])]});}
            var Q41;
            {var subQ1=sQuery(id+"F1.wireOp",EDGE,"E177");var subQ5=sQuery(id+"F1.wireOp",EDGE,"E173.4");var subQ6=makeQuery(id+"F1.imprint","INTERSECT",VERTEX,{"derivedFrom":[subQ5,subQ1]});Q41=makeQuery(id+"F1.imprint","IMPRINT",FACE,{"disambiguationData":[TD([[makeQuery(id+"F1.imprint","IMPRINT",EDGE,{"disambiguationData":[TD([[subQ6,-1.0]])],"derivedFrom":subQ5}),-1.0]])]});}
            var Q42;
            {var subQ1=sQuery(id+"F1.wireOp",EDGE,"E177");var subQ9=sQuery(id+"F1.wireOp",EDGE,"E173.4");var subQ10=makeQuery(id+"F1.imprint","INTERSECT",VERTEX,{"derivedFrom":[subQ9,subQ1]});Q42=makeQuery(id+"F1.imprint","IMPRINT",FACE,{"disambiguationData":[TD([[makeQuery(id+"F1.imprint","IMPRINT",EDGE,{"disambiguationData":[TD([[subQ10,-1.0]])],"derivedFrom":subQ9}),1.0]])]});}
            var Q43;
            {var subQ0=sQuery(id+"F1.wireOp",EDGE,"E191");var subQ1=sQuery(id+"F1.wireOp",EDGE,"E177");var subQ2=makeQuery(id+"F1.imprint","INTERSECT",VERTEX,{"disambiguationData":[OD(1.0)],"derivedFrom":[subQ1,subQ0]});Q43=makeQuery(id+"F1.imprint","IMPRINT",FACE,{"disambiguationData":[TD([[makeQuery(id+"F1.imprint","IMPRINT",EDGE,{"disambiguationData":[TD([[subQ2,-1.0]])],"derivedFrom":subQ1}),-1.0]])]});}
            var Q44;
            {var subQ1=sQuery(id+"F1.wireOp",EDGE,"E173.4");var subQ6=sQuery(id+"F1.wireOp",EDGE,"E176");var subQ8=makeQuery(id+"F1.imprint","INTERSECT",VERTEX,{"derivedFrom":[subQ1,subQ6]});Q44=makeQuery(id+"F1.imprint","IMPRINT",FACE,{"disambiguationData":[TD([[makeQuery(id+"F1.imprint","IMPRINT",EDGE,{"disambiguationData":[TD([[subQ8,-1.0]])],"derivedFrom":subQ1}),-1.0]])]});}
            var Q45;
            {var subQ0=sQuery(id+"F1.wireOp",EDGE,"E176");var subQ1=sQuery(id+"F1.wireOp",EDGE,"E173.4");var subQ2=makeQuery(id+"F1.imprint","INTERSECT",VERTEX,{"derivedFrom":[subQ1,subQ0]});Q45=makeQuery(id+"F1.imprint","IMPRINT",FACE,{"disambiguationData":[TD([[makeQuery(id+"F1.imprint","IMPRINT",EDGE,{"disambiguationData":[TD([[subQ2,-1.0]])],"derivedFrom":subQ1}),1.0]])]});}
            var Q46;
            {var subQ0=sQuery(id+"F1.wireOp",EDGE,"E182");var subQ1=sQuery(id+"F1.wireOp",EDGE,"E173.4");var subQ2=makeQuery(id+"F1.imprint","INTERSECT",VERTEX,{"disambiguationData":[OD(0.0)],"derivedFrom":[subQ1,subQ0]});Q46=makeQuery(id+"F1.imprint","IMPRINT",FACE,{"disambiguationData":[TD([[makeQuery(id+"F1.imprint","IMPRINT",EDGE,{"disambiguationData":[TD([[subQ2,-1.0]])],"derivedFrom":subQ1}),1.0]])]});}
            var Q47;
            {var subQ0=sQuery(id+"F1.wireOp",EDGE,"E182");var subQ1=sQuery(id+"F1.wireOp",EDGE,"E173.4");var subQ2=makeQuery(id+"F1.imprint","INTERSECT",VERTEX,{"disambiguationData":[OD(0.0)],"derivedFrom":[subQ1,subQ0]});Q47=makeQuery(id+"F1.imprint","IMPRINT",FACE,{"disambiguationData":[TD([[makeQuery(id+"F1.imprint","IMPRINT",EDGE,{"disambiguationData":[TD([[subQ2,-1.0]])],"derivedFrom":subQ1}),-1.0]])]});}
            var Q48;
            {var subQ1=sQuery(id+"F1.wireOp",EDGE,"E176");var subQ11=sQuery(id+"F1.wireOp",EDGE,"E173.3");var subQ12=makeQuery(id+"F1.imprint","INTERSECT",VERTEX,{"derivedFrom":[subQ11,subQ1]});Q48=makeQuery(id+"F1.imprint","IMPRINT",FACE,{"disambiguationData":[TD([[makeQuery(id+"F1.imprint","IMPRINT",EDGE,{"disambiguationData":[TD([[subQ12,-1.0]])],"derivedFrom":subQ11}),1.0]])]});}
            var Q49;
            {var subQ1=sQuery(id+"F1.wireOp",EDGE,"E176");var subQ3=sQuery(id+"F1.wireOp",EDGE,"E173.3");var subQ4=makeQuery(id+"F1.imprint","INTERSECT",VERTEX,{"derivedFrom":[subQ3,subQ1]});Q49=makeQuery(id+"F1.imprint","IMPRINT",FACE,{"disambiguationData":[TD([[makeQuery(id+"F1.imprint","IMPRINT",EDGE,{"disambiguationData":[TD([[subQ4,-1.0]])],"derivedFrom":subQ3}),-1.0]])]});}
            var Q50;
            {var subQ4=sQuery(id+"F1.wireOp",EDGE,"E183");var subQ5=sQuery(id+"F1.wireOp",EDGE,"E173.3");var subQ6=makeQuery(id+"F1.imprint","INTERSECT",VERTEX,{"disambiguationData":[OD(1.0)],"derivedFrom":[subQ5,subQ4]});Q50=makeQuery(id+"F1.imprint","IMPRINT",FACE,{"disambiguationData":[TD([[makeQuery(id+"F1.imprint","IMPRINT",EDGE,{"disambiguationData":[TD([[subQ6,-1.0]])],"derivedFrom":subQ5}),-1.0]])]});}
            var Q51;
            {var subQ0=sQuery(id+"F1.wireOp",EDGE,"E183");var subQ1=sQuery(id+"F1.wireOp",EDGE,"E173.3");var subQ2=makeQuery(id+"F1.imprint","INTERSECT",VERTEX,{"disambiguationData":[OD(1.0)],"derivedFrom":[subQ1,subQ0]});Q51=makeQuery(id+"F1.imprint","IMPRINT",FACE,{"disambiguationData":[TD([[makeQuery(id+"F1.imprint","IMPRINT",EDGE,{"disambiguationData":[TD([[subQ2,-1.0]])],"derivedFrom":subQ1}),1.0]])]});}
            var Q52;
            {var subQ0=sQuery(id+"F1.wireOp",EDGE,"E194");var subQ1=sQuery(id+"F1.wireOp",EDGE,"E176");var subQ2=makeQuery(id+"F1.imprint","INTERSECT",VERTEX,{"disambiguationData":[OD(1.0)],"derivedFrom":[subQ1,subQ0]});Q52=makeQuery(id+"F1.imprint","IMPRINT",FACE,{"disambiguationData":[TD([[makeQuery(id+"F1.imprint","IMPRINT",EDGE,{"disambiguationData":[TD([[subQ2,-1.0]])],"derivedFrom":subQ1}),-1.0]])]});}
            var Q53;
            {var subQ0=sQuery(id+"F1.wireOp",EDGE,"E183");var subQ1=sQuery(id+"F1.wireOp",EDGE,"E173.3");var subQ2=makeQuery(id+"F1.imprint","INTERSECT",VERTEX,{"disambiguationData":[OD(0.0)],"derivedFrom":[subQ1,subQ0]});Q53=makeQuery(id+"F1.imprint","IMPRINT",FACE,{"disambiguationData":[TD([[makeQuery(id+"F1.imprint","IMPRINT",EDGE,{"disambiguationData":[TD([[subQ2,-1.0]])],"derivedFrom":subQ1}),-1.0]])]});}
            var Q54;
            {var subQ0=sQuery(id+"F1.wireOp",EDGE,"E183");var subQ1=sQuery(id+"F1.wireOp",EDGE,"E173.3");var subQ2=makeQuery(id+"F1.imprint","INTERSECT",VERTEX,{"disambiguationData":[OD(0.0)],"derivedFrom":[subQ1,subQ0]});Q54=makeQuery(id+"F1.imprint","IMPRINT",FACE,{"disambiguationData":[TD([[makeQuery(id+"F1.imprint","IMPRINT",EDGE,{"disambiguationData":[TD([[subQ2,-1.0]])],"derivedFrom":subQ1}),1.0]])]});}
            var Q55;
            {var subQ0=sQuery(id+"F1.wireOp",EDGE,"E200");var subQ1=sQuery(id+"F1.wireOp",EDGE,"E174");var subQ2=makeQuery(id+"F1.imprint","INTERSECT",VERTEX,{"disambiguationData":[OD(1.0)],"derivedFrom":[subQ1,subQ0]});Q55=makeQuery(id+"F1.imprint","IMPRINT",FACE,{"disambiguationData":[TD([[makeQuery(id+"F1.imprint","IMPRINT",EDGE,{"disambiguationData":[TD([[subQ2,-1.0]])],"derivedFrom":subQ1}),-1.0]])]});}
            extrude(context, id + "F9", {"entities" : qUnion([Q0, Q1, Q2, Q3, Q4, Q5, Q6, Q7, Q8, Q9, Q10, Q11, Q12, Q13, Q14, Q15, Q16, Q17, Q18, Q19, Q20, Q21, Q22, Q23, Q24, Q25, Q26, Q27, Q28, Q29, Q30, Q31, Q32, Q33, Q34, Q35, Q36, Q37, Q38, Q39, Q40, Q41, Q42, Q43, Q44, Q45, Q46, Q47, Q48, Q49, Q50, Q51, Q52, Q53, Q54, Q55]), "depth" : 25.4 * mm});
        }
        {
            var Q0;
            {var subQ12=sQuery(id+"F1.wireOp",EDGE,"E185");var subQ14=makeQuery(id+"F1.imprint","INTERSECT",VERTEX,{"derivedFrom":[sQuery(id+"F1.wireOp",EDGE,"E180"),subQ12]});Q0=makeQuery(id+"F1.imprint","IMPRINT",FACE,{"disambiguationData":[TD([[makeQuery(id+"F1.imprint","IMPRINT",EDGE,{"disambiguationData":[TD([[subQ14,1.0]])],"derivedFrom":subQ12}),1.0]])]});}
            extrude(context, id + "F10", {"entities" : qUnion([Q0]), "depth" : 1778 * mm});
        }
        {
            var Q0;
            Q0=makeQuery(id+"F10.opExtrude","CAP_FACE",FACE,{"disambiguationData":[OSD([sQuery(id+"F1.wireOp",EDGE,"E185"),sQuery(id+"F1.wireOp",EDGE,"E188"),sQuery(id+"F1.wireOp",EDGE,"E191"),sQuery(id+"F1.wireOp",EDGE,"E194"),sQuery(id+"F1.wireOp",EDGE,"E197"),sQuery(id+"F1.wireOp",EDGE,"E200")])],"isStart":true});
            shell(context, id + "F11", {"entities" : qUnion([Q0]), "thickness" : 6.35 * mm});
        }
        {
            var Q0;
            {var subQ1=sQuery(id+"F1.wireOp",EDGE,"E169.4");var subQ3=sQuery(id+"F1.wireOp",EDGE,"E199");var subQ4=makeQuery(id+"F1.imprint","INTERSECT",VERTEX,{"derivedFrom":[subQ1,subQ3]});Q0=makeQuery(id+"F1.imprint","IMPRINT",FACE,{"disambiguationData":[TD([[makeQuery(id+"F1.imprint","IMPRINT",EDGE,{"disambiguationData":[TD([[subQ4,1.0]])],"derivedFrom":subQ3}),1.0]])]});}
            var Q1;
            {var subQ1=sQuery(id+"F1.wireOp",EDGE,"E169.4");var subQ3=sQuery(id+"F1.wireOp",EDGE,"E199");var subQ4=makeQuery(id+"F1.imprint","INTERSECT",VERTEX,{"derivedFrom":[subQ1,subQ3]});Q1=makeQuery(id+"F1.imprint","IMPRINT",FACE,{"disambiguationData":[TD([[makeQuery(id+"F1.imprint","IMPRINT",EDGE,{"disambiguationData":[TD([[subQ4,-1.0]])],"derivedFrom":subQ3}),1.0]])]});}
            var Q2;
            {var subQ1=sQuery(id+"F1.wireOp",EDGE,"E173.2");var subQ3=sQuery(id+"F1.wireOp",EDGE,"E199");var subQ4=makeQuery(id+"F1.imprint","INTERSECT",VERTEX,{"derivedFrom":[subQ1,subQ3]});Q2=makeQuery(id+"F1.imprint","IMPRINT",FACE,{"disambiguationData":[TD([[makeQuery(id+"F1.imprint","IMPRINT",EDGE,{"disambiguationData":[TD([[subQ4,-1.0]])],"derivedFrom":subQ3}),1.0]])]});}
            extrude(context, id + "F12", {"entities" : qUnion([Q0, Q1, Q2]), "depth" : 1790.7 * mm, "hasSecondDirection" : true, "secondDirectionOppositeDirection" : true, "secondDirectionDepth" : 12.7 * mm});
        }
        {
            var Q0;
            {var subQ0=sQuery(id+"F1.wireOp",EDGE,"E180");var subQ1=sQuery(id+"F1.wireOp",EDGE,"E173.0");var subQ2=makeQuery(id+"F1.imprint","INTERSECT",VERTEX,{"disambiguationData":[OD(1.0)],"derivedFrom":[subQ1,subQ0]});Q0=makeQuery(id+"F1.imprint","IMPRINT",FACE,{"disambiguationData":[TD([[makeQuery(id+"F1.imprint","IMPRINT",EDGE,{"disambiguationData":[TD([[subQ2,-1.0]])],"derivedFrom":subQ1}),1.0]])]});}
            var sketch = newSketch(context, id + "F13", { "sketchPlane" : qUnion([Q0])});
            skLineSegment(sketch, "E242.bottom", {"start": v(5413.1, 2959.24) * mm, "end": v(5438.5, 2959.24) * mm});
            skLineSegment(sketch, "E242.top", {"start": v(5413.1, 3067.28) * mm, "end": v(5438.5, 3067.28) * mm});
            skLineSegment(sketch, "E242.left", {"start": v(5413.1, 2959.24) * mm, "end": v(5413.1, 3067.28) * mm});
            skLineSegment(sketch, "E242.right", {"start": v(5438.5, 2959.24) * mm, "end": v(5438.5, 3067.28) * mm});
            skPoint(sketch, "E242.middle", {"position": v(5425.8, 3013.26) * mm});
            skLineSegment(sketch, "E243", {"start": v(5438.5, 3040.8) * mm, "end": v(5413.1, 3040.8) * mm});
            skSolve(sketch);
        }
        {
            var Q0;
            {var subQ1=sQuery(id+"F13.wireOp",EDGE,"E242.bottom");Q0=makeQuery(id+"F13.imprint","IMPRINT",FACE,{"disambiguationData":[TD([[makeQuery(id+"F13.imprint","IMPRINT",EDGE,{"derivedFrom":subQ1}),1.0]])]});}
            extrude(context, id + "F14", {"entities" : qUnion([Q0]), "depth" : 1778 * mm});
        }
    });
